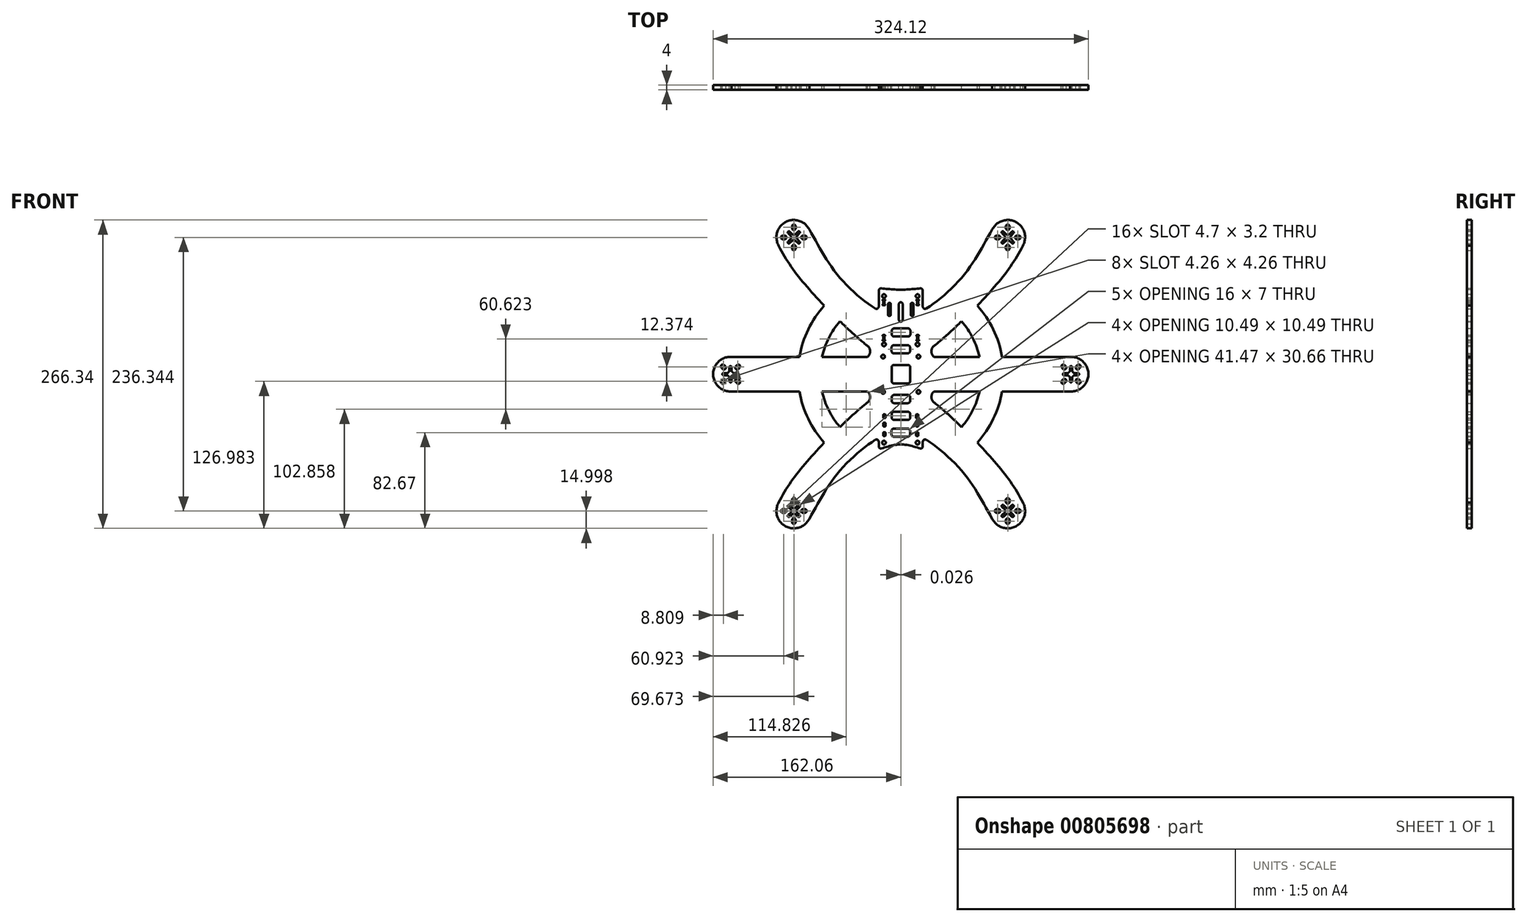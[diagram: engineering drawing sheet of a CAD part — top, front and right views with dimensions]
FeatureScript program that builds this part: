
annotation { "Feature Type Name" : "Feature", "Feature Type Description" : "" }
export const myFeature = defineFeature(function(context is Context, id is Id, definition is map)
    precondition{}
    {
        {
            var Q0;
            Q0=qCreatedBy(makeId("Front.planeOp"),FACE);
            var sketch = newSketch(context, id + "F0", { "sketchPlane" : qUnion([Q0])});
            skLineSegment(sketch, "E0", {"start": v(-266.59, 0) * mm, "end": v(301.68, 0) * mm, "construction": true});
            skCircle(sketch, "E1", {"center": v(-147.06, 0) * mm, "radius": 64.5 * mm, "construction": true});
            skLineSegment(sketch, "E2", {"start": v(0, 169.83) * mm, "end": v(0, -155.18) * mm, "construction": true});
            skCircle(sketch, "E3", {"center": v(-92.39, 118.17) * mm, "radius": 64.5 * mm, "construction": true});
            skCircle(sketch, "E4.MirrorC", {"center": v(-92.39, -118.17) * mm, "radius": 64.5 * mm, "construction": true});
            skCircle(sketch, "E5.MirrorC", {"center": v(92.39, 118.17) * mm, "radius": 64.5 * mm, "construction": true});
            skCircle(sketch, "E6.MirrorC", {"center": v(147.06, 0) * mm, "radius": 64.5 * mm, "construction": true});
            skCircle(sketch, "E7.MirrorC", {"center": v(92.39, -118.17) * mm, "radius": 64.5 * mm, "construction": true});
            skArc(sketch, "E8", {"start": v(-94.8, 118.82) * mm, "mid": v(-94.89, 118.17) * mm, "end": v(-94.8, 117.53) * mm});
            skCircle(sketch, "E9", {"center": v(-92.39, 118.17) * mm, "radius": 15 * mm});
            skArc(sketch, "E10", {"start": v(-148.31, 2.17) * mm, "mid": v(-148.83, 1.77) * mm, "end": v(-149.23, 1.25) * mm});
            skCircle(sketch, "E11", {"center": v(-147.06, 0) * mm, "radius": 15 * mm});
            skCircle(sketch, "E12.MirrorC", {"center": v(-92.39, -118.17) * mm, "radius": 2.5 * mm});
            skCircle(sketch, "E13.MirrorC", {"center": v(-92.39, -118.17) * mm, "radius": 15 * mm});
            skCircle(sketch, "E14.MirrorC", {"center": v(92.39, -118.17) * mm, "radius": 15 * mm});
            skCircle(sketch, "E15.MirrorC", {"center": v(92.39, -118.17) * mm, "radius": 2.5 * mm});
            skCircle(sketch, "E16.MirrorC", {"center": v(147.06, 0) * mm, "radius": 2.5 * mm});
            skCircle(sketch, "E17.MirrorC", {"center": v(147.06, 0) * mm, "radius": 15 * mm});
            skCircle(sketch, "E18.MirrorC", {"center": v(92.39, 118.17) * mm, "radius": 15 * mm});
            skCircle(sketch, "E19.MirrorC", {"center": v(92.39, 118.17) * mm, "radius": 2.5 * mm});
            skLineSegment(sketch, "E20", {"start": v(-92.39, 118.17) * mm, "end": v(92.39, -118.17) * mm, "construction": true});
            skLineSegment(sketch, "E21", {"start": v(92.39, 118.17) * mm, "end": v(-92.39, -118.17) * mm, "construction": true});
            skCircle(sketch, "E22", {"center": v(-15.25, 15.25) * mm, "radius": 1.6 * mm});
            skCircle(sketch, "E23.MirrorC", {"center": v(15.25, 15.25) * mm, "radius": 1.6 * mm});
            skCircle(sketch, "E24.MirrorC", {"center": v(-15.25, -15.25) * mm, "radius": 1.6 * mm});
            skCircle(sketch, "E25.MirrorC", {"center": v(15.25, -15.25) * mm, "radius": 1.6 * mm});
            skLineSegment(sketch, "E26.left", {"start": v(-19.03, 72.1) * mm, "end": v(-19.03, 58.42) * mm});
            skLineSegment(sketch, "E26.right", {"start": v(19.03, 72.1) * mm, "end": v(19.03, 58.42) * mm});
            skPoint(sketch, "E27.orphan", {"position": v(-6.44, 30.02) * mm});
            skLineSegment(sketch, "E28.MirrorCS", {"start": v(-105.57, -111.02) * mm, "end": v(-102.06, -106.7) * mm});
            skLineSegment(sketch, "E29.MirrorCS", {"start": v(-82.26, -129.24) * mm, "end": v(-79, -124.95) * mm});
            skLineSegment(sketch, "E30.MirrorCS", {"start": v(82.26, -129.24) * mm, "end": v(79.02, -124.99) * mm});
            skLineSegment(sketch, "E31.MirrorCS", {"start": v(105.57, -111.02) * mm, "end": v(102.06, -106.7) * mm});
            skPoint(sketch, "E32.orphan", {"position": v(19.03, 13.5) * mm});
            skPoint(sketch, "E33.orphan", {"position": v(19.03, -13.5) * mm});
            skPoint(sketch, "E34.orphan", {"position": v(-19.03, -13.5) * mm});
            skPoint(sketch, "E35.orphan", {"position": v(-19.03, 13.5) * mm});
            skFitSpline(sketch, "E36", {"points": [v(-105.57, 111.02) * mm, v(-74.34, 67.97) * mm, v(-29.36, 24.94) * mm], "startDerivative": vector(48.37, -95.71) * mm, "endDerivative": vector(65.9, -51.43) * mm});
            skFitSpline(sketch, "E37.MirrorCS", {"points": [v(105.57, 111.02) * mm, v(74.34, 67.97) * mm, v(29.36, 24.94) * mm], "startDerivative": vector(-48.37, -95.71) * mm, "endDerivative": vector(-65.9, -51.43) * mm});
            skFitSpline(sketch, "E38.MirrorCS", {"points": [v(-105.57, -111.02) * mm, v(-74.34, -67.97) * mm, v(-29.36, -24.94) * mm], "startDerivative": vector(48.37, 95.71) * mm, "endDerivative": vector(65.9, 51.43) * mm});
            skFitSpline(sketch, "E39.MirrorCS", {"points": [v(105.57, -111.02) * mm, v(74.34, -67.97) * mm, v(29.36, -24.94) * mm], "startDerivative": vector(-48.37, 95.71) * mm, "endDerivative": vector(-65.9, 51.43) * mm});
            skPoint(sketch, "E40.orphan", {"position": v(-27.58, -13.5) * mm});
            skPoint(sketch, "E41.trimOffspring.end.orphan", {"position": v(-27.58, 13.5) * mm});
            skPoint(sketch, "E42.orphan", {"position": v(27.58, -13.5) * mm});
            skPoint(sketch, "E43.trimOffspring.end.orphan", {"position": v(-19.03, -46.2) * mm});
            skPoint(sketch, "E44.orphan", {"position": v(19.03, -46.2) * mm});
            skPoint(sketch, "E45.trimOffspring.end.orphan", {"position": v(19.03, 46.2) * mm});
            skPoint(sketch, "E46.trimOffspring.end.orphan", {"position": v(-19.03, 46.2) * mm});
            skFitSpline(sketch, "E47", {"points": [v(-79.04, 125.02) * mm, v(-55.76, 87.28) * mm, v(-19.03, 54.92) * mm], "startDerivative": vector(44.52, -76.54) * mm, "endDerivative": vector(68.07, -37.92) * mm});
            skFitSpline(sketch, "E48.MirrorCS", {"points": [v(79.04, 125.02) * mm, v(55.76, 87.28) * mm, v(19.03, 54.92) * mm], "startDerivative": vector(-44.52, -76.54) * mm, "endDerivative": vector(-68.07, -37.92) * mm});
            skFitSpline(sketch, "E49.MirrorCS", {"points": [v(-79.04, -125.02) * mm, v(-55.76, -87.28) * mm, v(-19.03, -54.92) * mm], "startDerivative": vector(44.52, 76.54) * mm, "endDerivative": vector(68.07, 37.92) * mm});
            skFitSpline(sketch, "E50.MirrorCS", {"points": [v(79.04, -125.02) * mm, v(55.76, -87.28) * mm, v(19.03, -54.92) * mm], "startDerivative": vector(-44.52, 76.54) * mm, "endDerivative": vector(-68.07, 37.92) * mm});
            skPoint(sketch, "E51.orphan", {"position": v(27.58, 13.5) * mm});
            skLineSegment(sketch, "E52.trimOffspring", {"start": v(-19.03, -58.42) * mm, "end": v(-19.03, -62.32) * mm});
            skLineSegment(sketch, "E53.trimOffspring", {"start": v(19.03, -58.42) * mm, "end": v(19.03, -62.32) * mm});
            skArc(sketch, "E54.filletArc", {"start": v(-19.03, -58.42) * mm, "mid": v(-20.06, -56.67) * mm, "end": v(-22.09, -56.72) * mm});
            skArc(sketch, "E55.filletArc", {"start": v(22.09, -56.72) * mm, "mid": v(20.06, -56.67) * mm, "end": v(19.03, -58.42) * mm});
            skPoint(sketch, "E56.visualSharp", {"position": v(19.03, -64.32) * mm});
            skArc(sketch, "E56.filletArc", {"start": v(17.03, -64.32) * mm, "mid": v(18.44, -63.73) * mm, "end": v(19.03, -62.32) * mm});
            skPoint(sketch, "E57.visualSharp", {"position": v(-19.03, -64.32) * mm});
            skArc(sketch, "E57.filletArc", {"start": v(-19.03, -62.32) * mm, "mid": v(-18.44, -63.73) * mm, "end": v(-17.03, -64.32) * mm});
            skArc(sketch, "E58.filletArc", {"start": v(-22.09, 56.72) * mm, "mid": v(-20.06, 56.67) * mm, "end": v(-19.03, 58.42) * mm});
            skPoint(sketch, "E59.visualSharp", {"position": v(-19.03, 74.1) * mm});
            skArc(sketch, "E59.filletArc", {"start": v(-17.03, 74.1) * mm, "mid": v(-18.44, 73.51) * mm, "end": v(-19.03, 72.1) * mm});
            skPoint(sketch, "E60.visualSharp", {"position": v(19.03, 74.1) * mm});
            skArc(sketch, "E60.filletArc", {"start": v(19.03, 72.1) * mm, "mid": v(18.44, 73.51) * mm, "end": v(17.03, 74.1) * mm});
            skArc(sketch, "E61.filletArc", {"start": v(19.03, 58.42) * mm, "mid": v(20.06, 56.67) * mm, "end": v(22.09, 56.72) * mm});
            skFitSpline(sketch, "E62.trimOffspring", {"points": [v(-105.57, 111.02) * mm, v(-74.34, 67.97) * mm, v(-29.36, 24.94) * mm], "startDerivative": vector(48.37, -95.71) * mm, "endDerivative": vector(65.9, -51.43) * mm});
            skFitSpline(sketch, "E63.trimOffspring", {"points": [v(105.57, 111.02) * mm, v(74.34, 67.97) * mm, v(29.36, 24.94) * mm], "startDerivative": vector(-48.37, -95.71) * mm, "endDerivative": vector(-65.9, -51.43) * mm});
            skFitSpline(sketch, "E64.trimOffspring", {"points": [v(-105.57, -111.02) * mm, v(-74.34, -67.97) * mm, v(-29.36, -24.94) * mm], "startDerivative": vector(48.37, 95.71) * mm, "endDerivative": vector(65.9, 51.43) * mm});
            skFitSpline(sketch, "E65.trimOffspring", {"points": [v(105.57, -111.02) * mm, v(74.34, -67.97) * mm, v(29.36, -24.94) * mm], "startDerivative": vector(-48.37, 95.71) * mm, "endDerivative": vector(-65.9, 51.43) * mm});
            skCircle(sketch, "E66", {"center": v(-14.5, 67.5) * mm, "radius": 1.6 * mm});
            skCircle(sketch, "E67.MirrorC", {"center": v(14.5, 67.5) * mm, "radius": 1.6 * mm});
            skCircle(sketch, "E68", {"center": v(-14.5, 25.75) * mm, "radius": 1.6 * mm});
            skCircle(sketch, "E69.MirrorC", {"center": v(14.5, 25.75) * mm, "radius": 1.6 * mm});
            skCircle(sketch, "E70", {"center": v(-14.5, -59.12) * mm, "radius": 1.6 * mm});
            skCircle(sketch, "E71.MirrorC", {"center": v(14.5, -59.12) * mm, "radius": 1.6 * mm});
            skArc(sketch, "E72", {"start": v(-28.66, 14.98) * mm, "mid": v(-26.5, 20.27) * mm, "end": v(-29.56, 25.1) * mm});
            skArc(sketch, "E73.MirrorCS", {"start": v(28.66, 14.98) * mm, "mid": v(26.5, 20.27) * mm, "end": v(29.56, 25.1) * mm});
            skArc(sketch, "E74.MirrorCS", {"start": v(-28.66, -14.98) * mm, "mid": v(-26.5, -20.27) * mm, "end": v(-29.56, -25.1) * mm});
            skArc(sketch, "E75.MirrorCS", {"start": v(28.66, -14.98) * mm, "mid": v(26.5, -20.27) * mm, "end": v(29.56, -25.1) * mm});
            skLineSegment(sketch, "E76.bottom", {"start": v(-6, -47) * mm, "end": v(6, -47) * mm});
            skLineSegment(sketch, "E76.top", {"start": v(-6, -54) * mm, "end": v(6, -54) * mm});
            skLineSegment(sketch, "E76.left", {"start": v(-8, -49) * mm, "end": v(-8, -52) * mm});
            skLineSegment(sketch, "E76.right", {"start": v(8, -49) * mm, "end": v(8, -52) * mm});
            skLineSegment(sketch, "E77.bottom", {"start": v(-5.85, -32.5) * mm, "end": v(6.15, -32.5) * mm});
            skLineSegment(sketch, "E77.top", {"start": v(-5.85, -39.5) * mm, "end": v(6.15, -39.5) * mm});
            skLineSegment(sketch, "E77.left", {"start": v(-7.85, -34.5) * mm, "end": v(-7.85, -37.5) * mm});
            skLineSegment(sketch, "E77.right", {"start": v(8.15, -34.5) * mm, "end": v(8.15, -37.5) * mm});
            skLineSegment(sketch, "E78.bottom", {"start": v(-5.85, -18) * mm, "end": v(6.15, -18) * mm});
            skLineSegment(sketch, "E78.top", {"start": v(-5.85, -25) * mm, "end": v(6.15, -25) * mm});
            skLineSegment(sketch, "E78.left", {"start": v(-7.85, -20) * mm, "end": v(-7.85, -23) * mm});
            skLineSegment(sketch, "E78.right", {"start": v(8.15, -20) * mm, "end": v(8.15, -23) * mm});
            skLineSegment(sketch, "E79.bottom", {"start": v(-5.97, 25) * mm, "end": v(6.03, 25) * mm});
            skLineSegment(sketch, "E79.top", {"start": v(-5.97, 18) * mm, "end": v(6.03, 18) * mm});
            skLineSegment(sketch, "E79.left", {"start": v(-7.97, 23) * mm, "end": v(-7.97, 20) * mm});
            skLineSegment(sketch, "E79.right", {"start": v(8.03, 23) * mm, "end": v(8.03, 20) * mm});
            skLineSegment(sketch, "E80.bottom", {"start": v(-5.73, 39.5) * mm, "end": v(6.27, 39.5) * mm});
            skLineSegment(sketch, "E80.top", {"start": v(-5.73, 32.5) * mm, "end": v(6.27, 32.5) * mm});
            skLineSegment(sketch, "E80.left", {"start": v(-7.73, 37.5) * mm, "end": v(-7.73, 34.5) * mm});
            skLineSegment(sketch, "E80.right", {"start": v(8.27, 37.5) * mm, "end": v(8.27, 34.5) * mm});
            skLineSegment(sketch, "E81.bottom", {"start": v(-5.85, 8) * mm, "end": v(6.15, 8) * mm});
            skLineSegment(sketch, "E81.top", {"start": v(-5.85, -8) * mm, "end": v(6.15, -8) * mm});
            skLineSegment(sketch, "E81.left", {"start": v(-7.85, 6) * mm, "end": v(-7.85, -6) * mm});
            skLineSegment(sketch, "E81.right", {"start": v(8.15, 6) * mm, "end": v(8.15, -6) * mm});
            skPoint(sketch, "E82.visualSharp", {"position": v(-7.85, 8) * mm});
            skArc(sketch, "E82.filletArc", {"start": v(-5.85, 8) * mm, "mid": v(-7.26, 7.41) * mm, "end": v(-7.85, 6) * mm});
            skPoint(sketch, "E83.visualSharp", {"position": v(8.15, 8) * mm});
            skArc(sketch, "E83.filletArc", {"start": v(8.15, 6) * mm, "mid": v(7.56, 7.41) * mm, "end": v(6.15, 8) * mm});
            skPoint(sketch, "E84.visualSharp", {"position": v(8.15, -8) * mm});
            skArc(sketch, "E84.filletArc", {"start": v(6.15, -8) * mm, "mid": v(7.56, -7.41) * mm, "end": v(8.15, -6) * mm});
            skPoint(sketch, "E85.visualSharp", {"position": v(-7.85, -8) * mm});
            skArc(sketch, "E85.filletArc", {"start": v(-7.85, -6) * mm, "mid": v(-7.26, -7.41) * mm, "end": v(-5.85, -8) * mm});
            skPoint(sketch, "E86.visualSharp", {"position": v(8.15, -18) * mm});
            skArc(sketch, "E86.filletArc", {"start": v(8.15, -20) * mm, "mid": v(7.56, -18.59) * mm, "end": v(6.15, -18) * mm});
            skPoint(sketch, "E87.visualSharp", {"position": v(8.15, -25) * mm});
            skArc(sketch, "E87.filletArc", {"start": v(6.15, -25) * mm, "mid": v(7.56, -24.41) * mm, "end": v(8.15, -23) * mm});
            skPoint(sketch, "E88.visualSharp", {"position": v(-7.85, -25) * mm});
            skArc(sketch, "E88.filletArc", {"start": v(-7.85, -23) * mm, "mid": v(-7.26, -24.41) * mm, "end": v(-5.85, -25) * mm});
            skPoint(sketch, "E89.visualSharp", {"position": v(-7.85, -18) * mm});
            skArc(sketch, "E89.filletArc", {"start": v(-5.85, -18) * mm, "mid": v(-7.26, -18.59) * mm, "end": v(-7.85, -20) * mm});
            skPoint(sketch, "E90.visualSharp", {"position": v(8.15, -32.5) * mm});
            skArc(sketch, "E90.filletArc", {"start": v(8.15, -34.5) * mm, "mid": v(7.56, -33.09) * mm, "end": v(6.15, -32.5) * mm});
            skPoint(sketch, "E91.visualSharp", {"position": v(8.15, -39.5) * mm});
            skArc(sketch, "E91.filletArc", {"start": v(6.15, -39.5) * mm, "mid": v(7.56, -38.91) * mm, "end": v(8.15, -37.5) * mm});
            skPoint(sketch, "E92.visualSharp", {"position": v(-7.85, -39.5) * mm});
            skArc(sketch, "E92.filletArc", {"start": v(-7.85, -37.5) * mm, "mid": v(-7.26, -38.91) * mm, "end": v(-5.85, -39.5) * mm});
            skPoint(sketch, "E93.visualSharp", {"position": v(-7.85, -32.5) * mm});
            skArc(sketch, "E93.filletArc", {"start": v(-5.85, -32.5) * mm, "mid": v(-7.26, -33.09) * mm, "end": v(-7.85, -34.5) * mm});
            skPoint(sketch, "E94.visualSharp", {"position": v(8, -47) * mm});
            skArc(sketch, "E94.filletArc", {"start": v(8, -49) * mm, "mid": v(7.41, -47.59) * mm, "end": v(6, -47) * mm});
            skPoint(sketch, "E95.visualSharp", {"position": v(8, -54) * mm});
            skArc(sketch, "E95.filletArc", {"start": v(6, -54) * mm, "mid": v(7.41, -53.41) * mm, "end": v(8, -52) * mm});
            skPoint(sketch, "E96.visualSharp", {"position": v(-8, -54) * mm});
            skArc(sketch, "E96.filletArc", {"start": v(-8, -52) * mm, "mid": v(-7.41, -53.41) * mm, "end": v(-6, -54) * mm});
            skPoint(sketch, "E97.visualSharp", {"position": v(-8, -47) * mm});
            skArc(sketch, "E97.filletArc", {"start": v(-6, -47) * mm, "mid": v(-7.41, -47.59) * mm, "end": v(-8, -49) * mm});
            skPoint(sketch, "E98.visualSharp", {"position": v(8.03, 18) * mm});
            skArc(sketch, "E98.filletArc", {"start": v(6.03, 18) * mm, "mid": v(7.44, 18.59) * mm, "end": v(8.03, 20) * mm});
            skPoint(sketch, "E99.visualSharp", {"position": v(8.03, 25) * mm});
            skArc(sketch, "E99.filletArc", {"start": v(8.03, 23) * mm, "mid": v(7.44, 24.41) * mm, "end": v(6.03, 25) * mm});
            skPoint(sketch, "E100.visualSharp", {"position": v(-7.97, 25) * mm});
            skArc(sketch, "E100.filletArc", {"start": v(-5.97, 25) * mm, "mid": v(-7.39, 24.41) * mm, "end": v(-7.97, 23) * mm});
            skPoint(sketch, "E101.visualSharp", {"position": v(-7.97, 18) * mm});
            skArc(sketch, "E101.filletArc", {"start": v(-7.97, 20) * mm, "mid": v(-7.39, 18.59) * mm, "end": v(-5.97, 18) * mm});
            skPoint(sketch, "E102.visualSharp", {"position": v(8.27, 39.5) * mm});
            skArc(sketch, "E102.filletArc", {"start": v(8.27, 37.5) * mm, "mid": v(7.69, 38.91) * mm, "end": v(6.27, 39.5) * mm});
            skPoint(sketch, "E103.visualSharp", {"position": v(8.27, 32.5) * mm});
            skArc(sketch, "E103.filletArc", {"start": v(6.27, 32.5) * mm, "mid": v(7.69, 33.09) * mm, "end": v(8.27, 34.5) * mm});
            skPoint(sketch, "E104.visualSharp", {"position": v(-7.73, 32.5) * mm});
            skArc(sketch, "E104.filletArc", {"start": v(-7.73, 34.5) * mm, "mid": v(-7.14, 33.09) * mm, "end": v(-5.73, 32.5) * mm});
            skPoint(sketch, "E105.visualSharp", {"position": v(-7.73, 39.5) * mm});
            skArc(sketch, "E105.filletArc", {"start": v(-5.73, 39.5) * mm, "mid": v(-7.14, 38.91) * mm, "end": v(-7.73, 37.5) * mm});
            skCircle(sketch, "E106", {"center": v(-147.06, 0) * mm, "radius": 8 * mm, "construction": true});
            skCircle(sketch, "E107", {"center": v(-147.06, 0) * mm, "radius": 9.5 * mm, "construction": true});
            skCircle(sketch, "E108", {"center": v(-92.39, 118.17) * mm, "radius": 8 * mm, "construction": true});
            skCircle(sketch, "E109", {"center": v(-92.39, 118.17) * mm, "radius": 9.5 * mm, "construction": true});
            skPoint(sketch, "E110.MirrorCS.start.orphan", {"position": v(-82.26, 129.24) * mm});
            skPoint(sketch, "E111.MirrorCS.start.orphan", {"position": v(82.26, 129.24) * mm});
            skLineSegment(sketch, "E112", {"start": v(-147.82, 14.98) * mm, "end": v(-87.53, 14.98) * mm});
            skLineSegment(sketch, "E113.MirrorCS", {"start": v(-147.82, -14.98) * mm, "end": v(-87.53, -14.98) * mm});
            skLineSegment(sketch, "E114.MirrorCS", {"start": v(147.82, -14.98) * mm, "end": v(87.53, -14.98) * mm});
            skLineSegment(sketch, "E115.MirrorCS", {"start": v(147.82, 14.98) * mm, "end": v(87.53, 14.98) * mm});
            skLineSegment(sketch, "E116", {"start": v(-67.97, 14.98) * mm, "end": v(-28.66, 14.98) * mm});
            skPoint(sketch, "E117.orphan", {"position": v(-32.66, 13.5) * mm});
            skLineSegment(sketch, "E118.MirrorCS", {"start": v(-67.97, -14.98) * mm, "end": v(-28.66, -14.98) * mm});
            skPoint(sketch, "E119.orphan", {"position": v(-32.66, -13.5) * mm});
            skLineSegment(sketch, "E120.MirrorCS", {"start": v(67.97, 14.98) * mm, "end": v(28.66, 14.98) * mm});
            skLineSegment(sketch, "E121.MirrorCS", {"start": v(67.97, -14.98) * mm, "end": v(28.66, -14.98) * mm});
            skPoint(sketch, "E122.orphan", {"position": v(32.66, 13.5) * mm});
            skPoint(sketch, "E123.orphan", {"position": v(32.66, -13.5) * mm});
            skFitSpline(sketch, "E124", {"points": [v(-17.03, 74.1) * mm, v(0, 73.01) * mm, v(17.03, 74.1) * mm], "startDerivative": vector(34.06, -3.26) * mm, "endDerivative": vector(34.06, 3.26) * mm});
            skFitSpline(sketch, "E125", {"points": [v(-17.03, -64.32) * mm, v(0, -60.66) * mm, v(17.03, -64.32) * mm], "startDerivative": vector(34.06, 10.96) * mm, "endDerivative": vector(34.06, -10.96) * mm});
            skArc(sketch, "E126", {"start": v(1.6, 60.5) * mm, "mid": v(0, 62.1) * mm, "end": v(-1.6, 60.5) * mm});
            skArc(sketch, "E127", {"start": v(-1.6, 47) * mm, "mid": v(0, 45.4) * mm, "end": v(1.6, 47) * mm});
            skLineSegment(sketch, "E128", {"start": v(-1.6, 60.5) * mm, "end": v(-1.6, 47) * mm});
            skLineSegment(sketch, "E129.MirrorCS", {"start": v(1.6, 60.5) * mm, "end": v(1.6, 47) * mm});
            skPoint(sketch, "E130.center.orphan", {"position": v(0, 53.75) * mm});
            skLineSegment(sketch, "E131.bottom", {"start": v(-10.32, 61.42) * mm, "end": v(-9.32, 61.42) * mm});
            skLineSegment(sketch, "E131.top", {"start": v(-10.32, 50.42) * mm, "end": v(-9.32, 50.42) * mm});
            skLineSegment(sketch, "E131.left", {"start": v(-10.82, 60.92) * mm, "end": v(-10.82, 50.92) * mm});
            skLineSegment(sketch, "E131.right", {"start": v(-8.82, 60.92) * mm, "end": v(-8.82, 50.92) * mm});
            skPoint(sketch, "E132.visualSharp", {"position": v(-10.82, 61.42) * mm});
            skArc(sketch, "E132.filletArc", {"start": v(-10.32, 61.42) * mm, "mid": v(-10.68, 61.27) * mm, "end": v(-10.82, 60.92) * mm});
            skPoint(sketch, "E133.visualSharp", {"position": v(-8.82, 61.42) * mm});
            skArc(sketch, "E133.filletArc", {"start": v(-8.82, 60.92) * mm, "mid": v(-8.97, 61.27) * mm, "end": v(-9.32, 61.42) * mm});
            skPoint(sketch, "E134.visualSharp", {"position": v(-8.82, 50.42) * mm});
            skArc(sketch, "E134.filletArc", {"start": v(-9.32, 50.42) * mm, "mid": v(-8.97, 50.56) * mm, "end": v(-8.82, 50.92) * mm});
            skPoint(sketch, "E135.visualSharp", {"position": v(-10.82, 50.42) * mm});
            skArc(sketch, "E135.filletArc", {"start": v(-10.82, 50.92) * mm, "mid": v(-10.68, 50.56) * mm, "end": v(-10.32, 50.42) * mm});
            skArc(sketch, "E136.MirrorCS", {"start": v(8.82, 60.92) * mm, "mid": v(8.97, 61.27) * mm, "end": v(9.32, 61.42) * mm});
            skLineSegment(sketch, "E137.MirrorCS", {"start": v(10.32, 50.42) * mm, "end": v(9.32, 50.42) * mm});
            skLineSegment(sketch, "E138.MirrorCS", {"start": v(10.32, 61.42) * mm, "end": v(9.32, 61.42) * mm});
            skArc(sketch, "E139.MirrorCS", {"start": v(10.32, 61.42) * mm, "mid": v(10.68, 61.27) * mm, "end": v(10.82, 60.92) * mm});
            skArc(sketch, "E140.MirrorCS", {"start": v(9.32, 50.42) * mm, "mid": v(8.97, 50.56) * mm, "end": v(8.82, 50.92) * mm});
            skArc(sketch, "E141.MirrorCS", {"start": v(10.82, 50.92) * mm, "mid": v(10.68, 50.56) * mm, "end": v(10.32, 50.42) * mm});
            skLineSegment(sketch, "E142.MirrorCS", {"start": v(8.82, 60.92) * mm, "end": v(8.82, 50.92) * mm});
            skPoint(sketch, "E143.MirrorP", {"position": v(10.82, 61.42) * mm});
            skLineSegment(sketch, "E144.MirrorCS", {"start": v(10.82, 60.92) * mm, "end": v(10.82, 50.92) * mm});
            skPoint(sketch, "E145.MirrorP", {"position": v(8.82, 61.42) * mm});
            skPoint(sketch, "E146.MirrorP", {"position": v(10.82, 50.42) * mm});
            skPoint(sketch, "E147.MirrorP", {"position": v(8.82, 50.42) * mm});
            skCircle(sketch, "E148.MirrorC", {"center": v(92.39, 118.17) * mm, "radius": 9.5 * mm, "construction": true});
            skCircle(sketch, "E149.MirrorC", {"center": v(92.39, 118.17) * mm, "radius": 8 * mm, "construction": true});
            skCircle(sketch, "E150.MirrorC", {"center": v(-92.39, -118.17) * mm, "radius": 9.5 * mm, "construction": true});
            skCircle(sketch, "E151.MirrorC", {"center": v(-92.39, -118.17) * mm, "radius": 8 * mm, "construction": true});
            skCircle(sketch, "E152.MirrorC", {"center": v(92.39, -118.17) * mm, "radius": 9.5 * mm, "construction": true});
            skCircle(sketch, "E153.MirrorC", {"center": v(92.39, -118.17) * mm, "radius": 8 * mm, "construction": true});
            skCircle(sketch, "E154.MirrorC", {"center": v(147.06, 0) * mm, "radius": 9.5 * mm, "construction": true});
            skCircle(sketch, "E155.MirrorC", {"center": v(147.06, 0) * mm, "radius": 8 * mm, "construction": true});
            skPoint(sketch, "E156.orphan", {"position": v(-85.2, 14.98) * mm});
            skPoint(sketch, "E157.orphan", {"position": v(-85.2, -14.98) * mm});
            skPoint(sketch, "E158.orphan", {"position": v(85.2, -14.98) * mm});
            skArc(sketch, "E159", {"start": v(-67.97, -14.98) * mm, "mid": v(-62.18, -31.28) * mm, "end": v(-52.55, -45.64) * mm});
            skArc(sketch, "E160", {"start": v(-87.53, -14.98) * mm, "mid": v(-79.96, -38.63) * mm, "end": v(-66.14, -59.26) * mm});
            skPoint(sketch, "E161.orphan", {"position": v(-55.52, 48.54) * mm});
            skLineSegment(sketch, "E162.trimOffspring", {"start": v(-85.2, 14.98) * mm, "end": v(-84.33, 14.98) * mm});
            skLineSegment(sketch, "E163.trimOffspring", {"start": v(-85.2, -14.98) * mm, "end": v(-84.33, -14.98) * mm});
            skArc(sketch, "E164.trimOffspring", {"start": v(-52.55, 45.64) * mm, "mid": v(-62.18, 31.28) * mm, "end": v(-67.97, 14.98) * mm});
            skArc(sketch, "E165.trimOffspring", {"start": v(-66.14, 59.26) * mm, "mid": v(-79.96, 38.63) * mm, "end": v(-87.53, 14.98) * mm});
            skPoint(sketch, "E166.orphan", {"position": v(55.52, 48.54) * mm});
            skArc(sketch, "E167.trimOffspring", {"start": v(67.97, 14.98) * mm, "mid": v(62.18, 31.28) * mm, "end": v(52.55, 45.64) * mm});
            skArc(sketch, "E168.trimOffspring", {"start": v(87.53, 14.98) * mm, "mid": v(79.96, 38.63) * mm, "end": v(66.14, 59.26) * mm});
            skLineSegment(sketch, "E169.trimOffspring", {"start": v(85.2, 14.98) * mm, "end": v(84.33, 14.98) * mm});
            skLineSegment(sketch, "E170.trimOffspring", {"start": v(85.2, -14.98) * mm, "end": v(84.33, -14.98) * mm});
            skPoint(sketch, "E171.orphan", {"position": v(55.52, -48.54) * mm});
            skArc(sketch, "E172.trimOffspring", {"start": v(52.55, -45.64) * mm, "mid": v(62.18, -31.28) * mm, "end": v(67.97, -14.98) * mm});
            skArc(sketch, "E173.trimOffspring", {"start": v(66.14, -59.26) * mm, "mid": v(79.96, -38.63) * mm, "end": v(87.53, -14.98) * mm});
            skLineSegment(sketch, "E174", {"start": v(-147.06, 18.16) * mm, "end": v(-147.06, -18.32) * mm, "construction": true});
            skLineSegment(sketch, "E175", {"start": v(-163.44, 0) * mm, "end": v(-130.7, 0) * mm, "construction": true});
            skLineSegment(sketch, "E176", {"start": v(-162.22, -15.16) * mm, "end": v(-131.9, 15.16) * mm, "construction": true});
            skLineSegment(sketch, "E177.MirrorCS", {"start": v(-131.9, -15.16) * mm, "end": v(-162.22, 15.16) * mm, "construction": true});
            skArc(sketch, "E178", {"start": v(-146.06, 6) * mm, "mid": v(-147.06, 7) * mm, "end": v(-148.06, 6) * mm});
            skLineSegment(sketch, "E179", {"start": v(-148.06, 6) * mm, "end": v(-148.06, 2.6) * mm});
            skLineSegment(sketch, "E180.MirrorCS", {"start": v(-146.06, 6) * mm, "end": v(-146.06, 2.6) * mm});
            skLineSegment(sketch, "E181.MirrorCS", {"start": v(-148.06, -6) * mm, "end": v(-148.06, -2.6) * mm});
            skLineSegment(sketch, "E182.MirrorCS", {"start": v(-146.06, -6) * mm, "end": v(-146.06, -2.6) * mm});
            skArc(sketch, "E183.MirrorCS", {"start": v(-146.06, -6) * mm, "mid": v(-147.06, -7) * mm, "end": v(-148.06, -6) * mm});
            skArc(sketch, "E184", {"start": v(-141.06, -1) * mm, "mid": v(-140.06, 0) * mm, "end": v(-141.06, 1) * mm});
            skLineSegment(sketch, "E185", {"start": v(-141.06, 1) * mm, "end": v(-144.47, 1) * mm});
            skLineSegment(sketch, "E186.MirrorCS", {"start": v(-141.06, -1) * mm, "end": v(-144.77, -1) * mm});
            skLineSegment(sketch, "E187.MirrorCS", {"start": v(-141.06, -1) * mm, "end": v(-144.47, -1) * mm});
            skArc(sketch, "E188.trimOffspring", {"start": v(-144.9, 1.25) * mm, "mid": v(-145.3, 1.77) * mm, "end": v(-145.81, 2.17) * mm});
            skLineSegment(sketch, "E189.MirrorCS", {"start": v(-153.06, 1) * mm, "end": v(-149.66, 1) * mm});
            skArc(sketch, "E190.MirrorCS", {"start": v(-153.06, -1) * mm, "mid": v(-154.06, 0) * mm, "end": v(-153.06, 1) * mm});
            skLineSegment(sketch, "E191.MirrorCS", {"start": v(-153.06, -1) * mm, "end": v(-149.66, -1) * mm});
            skArc(sketch, "E192.trimOffspring", {"start": v(-149.23, -1.25) * mm, "mid": v(-148.83, -1.77) * mm, "end": v(-148.31, -2.17) * mm});
            skArc(sketch, "E193.trimOffspring", {"start": v(-145.81, -2.17) * mm, "mid": v(-145.3, -1.77) * mm, "end": v(-144.9, -1.25) * mm});
            skPoint(sketch, "E194.visualSharp", {"position": v(-148.06, 2.3) * mm});
            skArc(sketch, "E194.filletArc", {"start": v(-148.31, 2.17) * mm, "mid": v(-148.13, 2.35) * mm, "end": v(-148.06, 2.6) * mm});
            skPoint(sketch, "E195.visualSharp", {"position": v(-149.36, 1) * mm});
            skArc(sketch, "E195.filletArc", {"start": v(-149.66, 1) * mm, "mid": v(-149.41, 1.07) * mm, "end": v(-149.23, 1.25) * mm});
            skPoint(sketch, "E196.visualSharp", {"position": v(-149.36, -1) * mm});
            skArc(sketch, "E196.filletArc", {"start": v(-149.23, -1.25) * mm, "mid": v(-149.41, -1.07) * mm, "end": v(-149.66, -1) * mm});
            skPoint(sketch, "E197.visualSharp", {"position": v(-148.06, -2.3) * mm});
            skArc(sketch, "E197.filletArc", {"start": v(-148.06, -2.6) * mm, "mid": v(-148.13, -2.35) * mm, "end": v(-148.31, -2.17) * mm});
            skPoint(sketch, "E198.visualSharp", {"position": v(-146.06, -2.3) * mm});
            skArc(sketch, "E198.filletArc", {"start": v(-145.81, -2.17) * mm, "mid": v(-146, -2.35) * mm, "end": v(-146.06, -2.6) * mm});
            skPoint(sketch, "E199.visualSharp", {"position": v(-144.77, -1) * mm});
            skArc(sketch, "E199.filletArc", {"start": v(-144.47, -1) * mm, "mid": v(-144.72, -1.07) * mm, "end": v(-144.9, -1.25) * mm});
            skPoint(sketch, "E200.visualSharp", {"position": v(-144.77, 1) * mm});
            skArc(sketch, "E200.filletArc", {"start": v(-144.9, 1.25) * mm, "mid": v(-144.72, 1.07) * mm, "end": v(-144.47, 1) * mm});
            skPoint(sketch, "E201.visualSharp", {"position": v(-146.06, 2.3) * mm});
            skArc(sketch, "E201.filletArc", {"start": v(-146.06, 2.6) * mm, "mid": v(-146, 2.35) * mm, "end": v(-145.81, 2.17) * mm});
            skArc(sketch, "E202", {"start": v(-152.65, 7.85) * mm, "mid": v(-154.91, 7.85) * mm, "end": v(-154.91, 5.59) * mm});
            skLineSegment(sketch, "E203", {"start": v(-152.65, 7.85) * mm, "end": v(-151.59, 6.79) * mm});
            skLineSegment(sketch, "E204.MirrorCS", {"start": v(-154.91, 5.59) * mm, "end": v(-153.85, 4.53) * mm});
            skArc(sketch, "E205.trimOffspring", {"start": v(-153.85, 4.53) * mm, "mid": v(-151.59, 4.53) * mm, "end": v(-151.59, 6.79) * mm});
            skArc(sketch, "E206.MirrorCS", {"start": v(-141.48, 7.85) * mm, "mid": v(-139.22, 7.85) * mm, "end": v(-139.22, 5.59) * mm});
            skLineSegment(sketch, "E207.MirrorCS", {"start": v(-141.48, 7.85) * mm, "end": v(-142.54, 6.79) * mm});
            skLineSegment(sketch, "E208.MirrorCS", {"start": v(-139.22, 5.59) * mm, "end": v(-140.28, 4.53) * mm});
            skArc(sketch, "E209.MirrorCS", {"start": v(-140.28, 4.53) * mm, "mid": v(-142.54, 4.53) * mm, "end": v(-142.54, 6.79) * mm});
            skArc(sketch, "E210.MirrorCS", {"start": v(-152.65, -7.85) * mm, "mid": v(-154.91, -7.85) * mm, "end": v(-154.91, -5.59) * mm});
            skLineSegment(sketch, "E211.MirrorCS", {"start": v(-154.91, -5.59) * mm, "end": v(-153.85, -4.53) * mm});
            skArc(sketch, "E212.MirrorCS", {"start": v(-153.85, -4.53) * mm, "mid": v(-151.59, -4.53) * mm, "end": v(-151.59, -6.79) * mm});
            skLineSegment(sketch, "E213.MirrorCS", {"start": v(-152.65, -7.85) * mm, "end": v(-151.59, -6.79) * mm});
            skLineSegment(sketch, "E214.MirrorCS", {"start": v(-141.48, -7.85) * mm, "end": v(-142.54, -6.79) * mm});
            skArc(sketch, "E215.MirrorCS", {"start": v(-140.28, -4.53) * mm, "mid": v(-142.54, -4.53) * mm, "end": v(-142.54, -6.79) * mm});
            skLineSegment(sketch, "E216.MirrorCS", {"start": v(-139.22, -5.59) * mm, "end": v(-140.28, -4.53) * mm});
            skArc(sketch, "E217.MirrorCS", {"start": v(-141.48, -7.85) * mm, "mid": v(-139.22, -7.85) * mm, "end": v(-139.22, -5.59) * mm});
            skArc(sketch, "E218.MirrorCS", {"start": v(145.81, -2.17) * mm, "mid": v(146, -2.35) * mm, "end": v(146.06, -2.6) * mm});
            skArc(sketch, "E219.MirrorCS", {"start": v(144.47, -1) * mm, "mid": v(144.72, -1.07) * mm, "end": v(144.9, -1.25) * mm});
            skArc(sketch, "E220.MirrorCS", {"start": v(144.9, 1.25) * mm, "mid": v(144.72, 1.07) * mm, "end": v(144.47, 1) * mm});
            skArc(sketch, "E221.MirrorCS", {"start": v(148.31, 2.17) * mm, "mid": v(148.83, 1.77) * mm, "end": v(149.23, 1.25) * mm});
            skArc(sketch, "E222.MirrorCS", {"start": v(148.06, -2.6) * mm, "mid": v(148.13, -2.35) * mm, "end": v(148.31, -2.17) * mm});
            skArc(sketch, "E223.MirrorCS", {"start": v(145.81, -2.17) * mm, "mid": v(145.3, -1.77) * mm, "end": v(144.9, -1.25) * mm});
            skArc(sketch, "E224.MirrorCS", {"start": v(144.9, 1.25) * mm, "mid": v(145.3, 1.77) * mm, "end": v(145.81, 2.17) * mm});
            skArc(sketch, "E225.MirrorCS", {"start": v(149.23, -1.25) * mm, "mid": v(149.41, -1.07) * mm, "end": v(149.66, -1) * mm});
            skArc(sketch, "E226.MirrorCS", {"start": v(146.06, 2.6) * mm, "mid": v(146, 2.35) * mm, "end": v(145.81, 2.17) * mm});
            skArc(sketch, "E227.MirrorCS", {"start": v(149.23, -1.25) * mm, "mid": v(148.83, -1.77) * mm, "end": v(148.31, -2.17) * mm});
            skArc(sketch, "E228.MirrorCS", {"start": v(149.66, 1) * mm, "mid": v(149.41, 1.07) * mm, "end": v(149.23, 1.25) * mm});
            skArc(sketch, "E229.MirrorCS", {"start": v(148.31, 2.17) * mm, "mid": v(148.13, 2.35) * mm, "end": v(148.06, 2.6) * mm});
            skLineSegment(sketch, "E230.MirrorCS", {"start": v(152.65, 7.85) * mm, "end": v(151.59, 6.79) * mm});
            skLineSegment(sketch, "E231.MirrorCS", {"start": v(139.22, 5.59) * mm, "end": v(140.28, 4.53) * mm});
            skLineSegment(sketch, "E232.MirrorCS", {"start": v(154.91, 5.59) * mm, "end": v(153.85, 4.53) * mm});
            skLineSegment(sketch, "E233.MirrorCS", {"start": v(141.06, -1) * mm, "end": v(144.77, -1) * mm});
            skLineSegment(sketch, "E234.MirrorCS", {"start": v(153.06, -1) * mm, "end": v(149.66, -1) * mm});
            skLineSegment(sketch, "E235.MirrorCS", {"start": v(148.06, -6) * mm, "end": v(148.06, -2.6) * mm});
            skLineSegment(sketch, "E236.MirrorCS", {"start": v(148.06, 6) * mm, "end": v(148.06, 2.6) * mm});
            skLineSegment(sketch, "E237.MirrorCS", {"start": v(141.48, -7.85) * mm, "end": v(142.54, -6.79) * mm});
            skLineSegment(sketch, "E238.MirrorCS", {"start": v(146.06, -6) * mm, "end": v(146.06, -2.6) * mm});
            skArc(sketch, "E239.MirrorCS", {"start": v(140.28, -4.53) * mm, "mid": v(142.54, -4.53) * mm, "end": v(142.54, -6.79) * mm});
            skLineSegment(sketch, "E240.MirrorCS", {"start": v(153.06, 1) * mm, "end": v(149.66, 1) * mm});
            skPoint(sketch, "E241.MirrorP", {"position": v(149.36, -1) * mm});
            skPoint(sketch, "E242.MirrorP", {"position": v(148.06, 2.3) * mm});
            skArc(sketch, "E243.MirrorCS", {"start": v(152.65, 7.85) * mm, "mid": v(154.91, 7.85) * mm, "end": v(154.91, 5.59) * mm});
            skPoint(sketch, "E244.MirrorP", {"position": v(148.06, -2.3) * mm});
            skArc(sketch, "E245.MirrorCS", {"start": v(153.06, -1) * mm, "mid": v(154.06, 0) * mm, "end": v(153.06, 1) * mm});
            skLineSegment(sketch, "E246.MirrorCS", {"start": v(141.06, -1) * mm, "end": v(144.47, -1) * mm});
            skPoint(sketch, "E247.MirrorP", {"position": v(146.06, -2.3) * mm});
            skPoint(sketch, "E248.MirrorP", {"position": v(146.06, 2.3) * mm});
            skLineSegment(sketch, "E249.MirrorCS", {"start": v(152.65, -7.85) * mm, "end": v(151.59, -6.79) * mm});
            skArc(sketch, "E250.MirrorCS", {"start": v(146.06, -6) * mm, "mid": v(147.06, -7) * mm, "end": v(148.06, -6) * mm});
            skLineSegment(sketch, "E251.MirrorCS", {"start": v(141.48, 7.85) * mm, "end": v(142.54, 6.79) * mm});
            skArc(sketch, "E252.MirrorCS", {"start": v(153.85, 4.53) * mm, "mid": v(151.59, 4.53) * mm, "end": v(151.59, 6.79) * mm});
            skArc(sketch, "E253.MirrorCS", {"start": v(140.28, 4.53) * mm, "mid": v(142.54, 4.53) * mm, "end": v(142.54, 6.79) * mm});
            skLineSegment(sketch, "E254.MirrorCS", {"start": v(146.06, 6) * mm, "end": v(146.06, 2.6) * mm});
            skArc(sketch, "E255.MirrorCS", {"start": v(153.85, -4.53) * mm, "mid": v(151.59, -4.53) * mm, "end": v(151.59, -6.79) * mm});
            skArc(sketch, "E256.MirrorCS", {"start": v(141.48, -7.85) * mm, "mid": v(139.22, -7.85) * mm, "end": v(139.22, -5.59) * mm});
            skLineSegment(sketch, "E257.MirrorCS", {"start": v(141.06, 1) * mm, "end": v(144.47, 1) * mm});
            skArc(sketch, "E258.MirrorCS", {"start": v(141.06, -1) * mm, "mid": v(140.06, 0) * mm, "end": v(141.06, 1) * mm});
            skLineSegment(sketch, "E259.MirrorCS", {"start": v(154.91, -5.59) * mm, "end": v(153.85, -4.53) * mm});
            skLineSegment(sketch, "E260.MirrorCS", {"start": v(139.22, -5.59) * mm, "end": v(140.28, -4.53) * mm});
            skPoint(sketch, "E261.MirrorP", {"position": v(144.77, -1) * mm});
            skPoint(sketch, "E262.MirrorP", {"position": v(149.36, 1) * mm});
            skPoint(sketch, "E263.MirrorP", {"position": v(144.77, 1) * mm});
            skArc(sketch, "E264.MirrorCS", {"start": v(152.65, -7.85) * mm, "mid": v(154.91, -7.85) * mm, "end": v(154.91, -5.59) * mm});
            skArc(sketch, "E265.MirrorCS", {"start": v(141.48, 7.85) * mm, "mid": v(139.22, 7.85) * mm, "end": v(139.22, 5.59) * mm});
            skArc(sketch, "E266.MirrorCS", {"start": v(146.06, 6) * mm, "mid": v(147.06, 7) * mm, "end": v(148.06, 6) * mm});
            skLineSegment(sketch, "E267", {"start": v(-15.21, 33.8) * mm, "end": v(-14.1, 33.8) * mm});
            skLineSegment(sketch, "E268", {"start": v(-13.6, 33.3) * mm, "end": v(-13.6, 33.3) * mm});
            skLineSegment(sketch, "E269", {"start": v(-14.1, 32.8) * mm, "end": v(-14.15, 32.8) * mm});
            skLineSegment(sketch, "E270", {"start": v(-14.15, 32.8) * mm, "end": v(-14.15, 29.76) * mm});
            skLineSegment(sketch, "E271", {"start": v(-14.15, 29.76) * mm, "end": v(-14.1, 29.76) * mm});
            skLineSegment(sketch, "E272", {"start": v(-13.6, 29.26) * mm, "end": v(-13.6, 29.26) * mm});
            skLineSegment(sketch, "E273", {"start": v(-14.1, 28.76) * mm, "end": v(-15.21, 28.76) * mm});
            skLineSegment(sketch, "E274", {"start": v(-15.71, 29.26) * mm, "end": v(-15.71, 29.26) * mm});
            skLineSegment(sketch, "E275", {"start": v(-15.21, 29.76) * mm, "end": v(-15.15, 29.76) * mm});
            skLineSegment(sketch, "E276", {"start": v(-15.15, 29.76) * mm, "end": v(-15.15, 32.8) * mm});
            skLineSegment(sketch, "E277", {"start": v(-15.15, 32.8) * mm, "end": v(-15.21, 32.8) * mm});
            skLineSegment(sketch, "E278", {"start": v(-15.71, 33.3) * mm, "end": v(-15.71, 33.3) * mm});
            skPoint(sketch, "E279.visualSharp", {"position": v(-15.71, 33.8) * mm});
            skArc(sketch, "E279.filletArc", {"start": v(-15.21, 33.8) * mm, "mid": v(-15.56, 33.65) * mm, "end": v(-15.71, 33.3) * mm});
            skPoint(sketch, "E280.visualSharp", {"position": v(-15.71, 32.8) * mm});
            skArc(sketch, "E280.filletArc", {"start": v(-15.71, 33.3) * mm, "mid": v(-15.56, 32.94) * mm, "end": v(-15.21, 32.8) * mm});
            skPoint(sketch, "E281.visualSharp", {"position": v(-13.6, 33.8) * mm});
            skArc(sketch, "E281.filletArc", {"start": v(-13.6, 33.3) * mm, "mid": v(-13.74, 33.65) * mm, "end": v(-14.1, 33.8) * mm});
            skPoint(sketch, "E282.visualSharp", {"position": v(-13.6, 32.8) * mm});
            skArc(sketch, "E282.filletArc", {"start": v(-14.1, 32.8) * mm, "mid": v(-13.74, 32.94) * mm, "end": v(-13.6, 33.3) * mm});
            skPoint(sketch, "E283.visualSharp", {"position": v(-13.6, 29.76) * mm});
            skArc(sketch, "E283.filletArc", {"start": v(-13.6, 29.26) * mm, "mid": v(-13.74, 29.62) * mm, "end": v(-14.1, 29.76) * mm});
            skPoint(sketch, "E284.visualSharp", {"position": v(-13.6, 28.76) * mm});
            skArc(sketch, "E284.filletArc", {"start": v(-14.1, 28.76) * mm, "mid": v(-13.74, 28.9) * mm, "end": v(-13.6, 29.26) * mm});
            skPoint(sketch, "E285.visualSharp", {"position": v(-15.71, 29.76) * mm});
            skArc(sketch, "E285.filletArc", {"start": v(-15.21, 29.76) * mm, "mid": v(-15.56, 29.62) * mm, "end": v(-15.71, 29.26) * mm});
            skPoint(sketch, "E286.visualSharp", {"position": v(-15.71, 28.76) * mm});
            skArc(sketch, "E286.filletArc", {"start": v(-15.71, 29.26) * mm, "mid": v(-15.56, 28.9) * mm, "end": v(-15.21, 28.76) * mm});
            skLineSegment(sketch, "E287", {"start": v(-29.23, 46.63) * mm, "end": v(29.48, 46.63) * mm, "construction": true});
            skLineSegment(sketch, "E288.MirrorCS", {"start": v(-14.15, 63.5) * mm, "end": v(-14.1, 63.5) * mm});
            skArc(sketch, "E289.MirrorCS", {"start": v(-14.1, 60.47) * mm, "mid": v(-13.74, 60.32) * mm, "end": v(-13.6, 59.97) * mm});
            skArc(sketch, "E290.MirrorCS", {"start": v(-13.6, 59.97) * mm, "mid": v(-13.74, 59.62) * mm, "end": v(-14.1, 59.47) * mm});
            skArc(sketch, "E291.MirrorCS", {"start": v(-15.71, 59.97) * mm, "mid": v(-15.56, 60.32) * mm, "end": v(-15.21, 60.47) * mm});
            skArc(sketch, "E292.MirrorCS", {"start": v(-15.21, 59.47) * mm, "mid": v(-15.56, 59.62) * mm, "end": v(-15.71, 59.97) * mm});
            skLineSegment(sketch, "E293.MirrorCS", {"start": v(-15.15, 60.47) * mm, "end": v(-15.21, 60.47) * mm});
            skLineSegment(sketch, "E294.MirrorCS", {"start": v(-15.21, 63.5) * mm, "end": v(-15.15, 63.5) * mm});
            skLineSegment(sketch, "E295.MirrorCS", {"start": v(-14.1, 60.47) * mm, "end": v(-14.15, 60.47) * mm});
            skLineSegment(sketch, "E296.MirrorCS", {"start": v(-15.21, 59.47) * mm, "end": v(-14.1, 59.47) * mm});
            skArc(sketch, "E297.MirrorCS", {"start": v(-15.21, 63.5) * mm, "mid": v(-15.56, 63.65) * mm, "end": v(-15.71, 64) * mm});
            skArc(sketch, "E298.MirrorCS", {"start": v(-13.6, 64) * mm, "mid": v(-13.74, 63.65) * mm, "end": v(-14.1, 63.5) * mm});
            skLineSegment(sketch, "E299.MirrorCS", {"start": v(-14.1, 64.5) * mm, "end": v(-15.21, 64.5) * mm});
            skArc(sketch, "E300.MirrorCS", {"start": v(-15.71, 64) * mm, "mid": v(-15.56, 64.35) * mm, "end": v(-15.21, 64.5) * mm});
            skArc(sketch, "E301.MirrorCS", {"start": v(-14.1, 64.5) * mm, "mid": v(-13.74, 64.35) * mm, "end": v(-13.6, 64) * mm});
            skLineSegment(sketch, "E302.MirrorCS", {"start": v(-15.71, 59.97) * mm, "end": v(-15.71, 59.97) * mm});
            skLineSegment(sketch, "E303.MirrorCS", {"start": v(-15.71, 64) * mm, "end": v(-15.71, 64) * mm});
            skLineSegment(sketch, "E304.MirrorCS", {"start": v(-13.6, 64) * mm, "end": v(-13.6, 64) * mm});
            skLineSegment(sketch, "E305.MirrorCS", {"start": v(-13.6, 59.97) * mm, "end": v(-13.6, 59.97) * mm});
            skPoint(sketch, "E306.MirrorP", {"position": v(-15.71, 64.5) * mm});
            skPoint(sketch, "E307.MirrorP", {"position": v(-15.71, 63.5) * mm});
            skPoint(sketch, "E308.MirrorP", {"position": v(-13.6, 64.5) * mm});
            skLineSegment(sketch, "E309.MirrorCS", {"start": v(-15.15, 63.5) * mm, "end": v(-15.15, 60.47) * mm});
            skPoint(sketch, "E310.MirrorP", {"position": v(-13.6, 63.5) * mm});
            skPoint(sketch, "E311.MirrorP", {"position": v(-13.6, 60.47) * mm});
            skLineSegment(sketch, "E312.MirrorCS", {"start": v(-14.15, 60.47) * mm, "end": v(-14.15, 63.5) * mm});
            skPoint(sketch, "E313.MirrorP", {"position": v(-13.6, 59.47) * mm});
            skPoint(sketch, "E314.MirrorP", {"position": v(-15.71, 60.47) * mm});
            skPoint(sketch, "E315.MirrorP", {"position": v(-15.71, 59.47) * mm});
            skArc(sketch, "E316.MirrorCS", {"start": v(14.1, 60.47) * mm, "mid": v(13.74, 60.32) * mm, "end": v(13.6, 59.97) * mm});
            skArc(sketch, "E317.MirrorCS", {"start": v(13.6, 64) * mm, "mid": v(13.74, 63.65) * mm, "end": v(14.1, 63.5) * mm});
            skLineSegment(sketch, "E318.MirrorCS", {"start": v(14.15, 63.5) * mm, "end": v(14.1, 63.5) * mm});
            skArc(sketch, "E319.MirrorCS", {"start": v(15.71, 59.97) * mm, "mid": v(15.56, 60.32) * mm, "end": v(15.21, 60.47) * mm});
            skLineSegment(sketch, "E320.MirrorCS", {"start": v(15.15, 60.47) * mm, "end": v(15.21, 60.47) * mm});
            skLineSegment(sketch, "E321.MirrorCS", {"start": v(15.21, 63.5) * mm, "end": v(15.15, 63.5) * mm});
            skLineSegment(sketch, "E322.MirrorCS", {"start": v(14.1, 60.47) * mm, "end": v(14.15, 60.47) * mm});
            skArc(sketch, "E323.MirrorCS", {"start": v(15.21, 63.5) * mm, "mid": v(15.56, 63.65) * mm, "end": v(15.71, 64) * mm});
            skArc(sketch, "E324.MirrorCS", {"start": v(15.71, 64) * mm, "mid": v(15.56, 64.35) * mm, "end": v(15.21, 64.5) * mm});
            skArc(sketch, "E325.MirrorCS", {"start": v(14.1, 64.5) * mm, "mid": v(13.74, 64.35) * mm, "end": v(13.6, 64) * mm});
            skArc(sketch, "E326.MirrorCS", {"start": v(13.6, 59.97) * mm, "mid": v(13.74, 59.62) * mm, "end": v(14.1, 59.47) * mm});
            skArc(sketch, "E327.MirrorCS", {"start": v(15.21, 59.47) * mm, "mid": v(15.56, 59.62) * mm, "end": v(15.71, 59.97) * mm});
            skLineSegment(sketch, "E328.MirrorCS", {"start": v(15.71, 59.97) * mm, "end": v(15.71, 59.97) * mm});
            skLineSegment(sketch, "E329.MirrorCS", {"start": v(15.71, 64) * mm, "end": v(15.71, 64) * mm});
            skLineSegment(sketch, "E330.MirrorCS", {"start": v(13.6, 64) * mm, "end": v(13.6, 64) * mm});
            skLineSegment(sketch, "E331.MirrorCS", {"start": v(13.6, 59.97) * mm, "end": v(13.6, 59.97) * mm});
            skPoint(sketch, "E332.MirrorP", {"position": v(15.71, 59.47) * mm});
            skLineSegment(sketch, "E333.MirrorCS", {"start": v(14.1, 64.5) * mm, "end": v(15.21, 64.5) * mm});
            skLineSegment(sketch, "E334.MirrorCS", {"start": v(15.15, 63.5) * mm, "end": v(15.15, 60.47) * mm});
            skLineSegment(sketch, "E335.MirrorCS", {"start": v(14.15, 60.47) * mm, "end": v(14.15, 63.5) * mm});
            skPoint(sketch, "E336.MirrorP", {"position": v(15.71, 64.5) * mm});
            skPoint(sketch, "E337.MirrorP", {"position": v(15.71, 63.5) * mm});
            skPoint(sketch, "E338.MirrorP", {"position": v(13.6, 64.5) * mm});
            skPoint(sketch, "E339.MirrorP", {"position": v(13.6, 63.5) * mm});
            skPoint(sketch, "E340.MirrorP", {"position": v(13.6, 60.47) * mm});
            skLineSegment(sketch, "E341.MirrorCS", {"start": v(15.21, 59.47) * mm, "end": v(14.1, 59.47) * mm});
            skPoint(sketch, "E342.MirrorP", {"position": v(13.6, 59.47) * mm});
            skPoint(sketch, "E343.MirrorP", {"position": v(15.71, 60.47) * mm});
            skArc(sketch, "E344.MirrorCS", {"start": v(13.6, 29.26) * mm, "mid": v(13.74, 29.62) * mm, "end": v(14.1, 29.76) * mm});
            skArc(sketch, "E345.MirrorCS", {"start": v(14.1, 32.8) * mm, "mid": v(13.74, 32.94) * mm, "end": v(13.6, 33.3) * mm});
            skArc(sketch, "E346.MirrorCS", {"start": v(13.6, 33.3) * mm, "mid": v(13.74, 33.65) * mm, "end": v(14.1, 33.8) * mm});
            skArc(sketch, "E347.MirrorCS", {"start": v(15.71, 33.3) * mm, "mid": v(15.56, 32.94) * mm, "end": v(15.21, 32.8) * mm});
            skLineSegment(sketch, "E348.MirrorCS", {"start": v(15.15, 32.8) * mm, "end": v(15.21, 32.8) * mm});
            skLineSegment(sketch, "E349.MirrorCS", {"start": v(15.21, 29.76) * mm, "end": v(15.15, 29.76) * mm});
            skLineSegment(sketch, "E350.MirrorCS", {"start": v(14.1, 28.76) * mm, "end": v(15.21, 28.76) * mm});
            skLineSegment(sketch, "E351.MirrorCS", {"start": v(14.15, 29.76) * mm, "end": v(14.1, 29.76) * mm});
            skLineSegment(sketch, "E352.MirrorCS", {"start": v(14.1, 32.8) * mm, "end": v(14.15, 32.8) * mm});
            skArc(sketch, "E353.MirrorCS", {"start": v(15.21, 29.76) * mm, "mid": v(15.56, 29.62) * mm, "end": v(15.71, 29.26) * mm});
            skArc(sketch, "E354.MirrorCS", {"start": v(15.21, 33.8) * mm, "mid": v(15.56, 33.65) * mm, "end": v(15.71, 33.3) * mm});
            skArc(sketch, "E355.MirrorCS", {"start": v(15.71, 29.26) * mm, "mid": v(15.56, 28.9) * mm, "end": v(15.21, 28.76) * mm});
            skArc(sketch, "E356.MirrorCS", {"start": v(14.1, 28.76) * mm, "mid": v(13.74, 28.9) * mm, "end": v(13.6, 29.26) * mm});
            skLineSegment(sketch, "E357.MirrorCS", {"start": v(15.71, 33.3) * mm, "end": v(15.71, 33.3) * mm});
            skLineSegment(sketch, "E358.MirrorCS", {"start": v(15.71, 29.26) * mm, "end": v(15.71, 29.26) * mm});
            skLineSegment(sketch, "E359.MirrorCS", {"start": v(13.6, 29.26) * mm, "end": v(13.6, 29.26) * mm});
            skLineSegment(sketch, "E360.MirrorCS", {"start": v(13.6, 33.3) * mm, "end": v(13.6, 33.3) * mm});
            skPoint(sketch, "E361.MirrorP", {"position": v(15.71, 28.76) * mm});
            skPoint(sketch, "E362.MirrorP", {"position": v(15.71, 29.76) * mm});
            skPoint(sketch, "E363.MirrorP", {"position": v(13.6, 28.76) * mm});
            skLineSegment(sketch, "E364.MirrorCS", {"start": v(15.15, 29.76) * mm, "end": v(15.15, 32.8) * mm});
            skPoint(sketch, "E365.MirrorP", {"position": v(13.6, 29.76) * mm});
            skPoint(sketch, "E366.MirrorP", {"position": v(13.6, 32.8) * mm});
            skLineSegment(sketch, "E367.MirrorCS", {"start": v(14.15, 32.8) * mm, "end": v(14.15, 29.76) * mm});
            skPoint(sketch, "E368.MirrorP", {"position": v(13.6, 33.8) * mm});
            skLineSegment(sketch, "E369.MirrorCS", {"start": v(15.21, 33.8) * mm, "end": v(14.1, 33.8) * mm});
            skPoint(sketch, "E370.MirrorP", {"position": v(15.71, 32.8) * mm});
            skPoint(sketch, "E371.MirrorP", {"position": v(15.71, 33.8) * mm});
            skLineSegment(sketch, "E372.bottom", {"start": v(-14.65, -34.75) * mm, "end": v(-13.65, -34.75) * mm});
            skLineSegment(sketch, "E372.top", {"start": v(-14.65, -37.95) * mm, "end": v(-13.65, -37.95) * mm});
            skLineSegment(sketch, "E372.left", {"start": v(-15.15, -35.25) * mm, "end": v(-15.15, -37.45) * mm});
            skLineSegment(sketch, "E372.right", {"start": v(-13.15, -35.25) * mm, "end": v(-13.15, -37.45) * mm});
            skLineSegment(sketch, "E373.bottom", {"start": v(-14.65, -41.95) * mm, "end": v(-13.65, -41.95) * mm});
            skLineSegment(sketch, "E373.top", {"start": v(-14.65, -45.15) * mm, "end": v(-13.65, -45.15) * mm});
            skLineSegment(sketch, "E373.left", {"start": v(-15.15, -42.45) * mm, "end": v(-15.15, -44.65) * mm});
            skLineSegment(sketch, "E373.right", {"start": v(-13.15, -42.45) * mm, "end": v(-13.15, -44.65) * mm});
            skLineSegment(sketch, "E374.bottom", {"start": v(-14.65, -50.15) * mm, "end": v(-13.65, -50.15) * mm});
            skLineSegment(sketch, "E374.top", {"start": v(-14.65, -53.35) * mm, "end": v(-13.65, -53.35) * mm});
            skLineSegment(sketch, "E374.left", {"start": v(-15.15, -50.65) * mm, "end": v(-15.15, -52.85) * mm});
            skLineSegment(sketch, "E374.right", {"start": v(-13.15, -50.65) * mm, "end": v(-13.15, -52.85) * mm});
            skPoint(sketch, "E375.visualSharp", {"position": v(-15.15, -34.75) * mm});
            skArc(sketch, "E375.filletArc", {"start": v(-14.65, -34.75) * mm, "mid": v(-15, -34.9) * mm, "end": v(-15.15, -35.25) * mm});
            skPoint(sketch, "E376.visualSharp", {"position": v(-13.15, -34.75) * mm});
            skArc(sketch, "E376.filletArc", {"start": v(-13.15, -35.25) * mm, "mid": v(-13.3, -34.9) * mm, "end": v(-13.65, -34.75) * mm});
            skPoint(sketch, "E377.visualSharp", {"position": v(-13.15, -37.95) * mm});
            skArc(sketch, "E377.filletArc", {"start": v(-13.65, -37.95) * mm, "mid": v(-13.3, -37.8) * mm, "end": v(-13.15, -37.45) * mm});
            skPoint(sketch, "E378.visualSharp", {"position": v(-15.15, -37.95) * mm});
            skArc(sketch, "E378.filletArc", {"start": v(-15.15, -37.45) * mm, "mid": v(-15, -37.8) * mm, "end": v(-14.65, -37.95) * mm});
            skPoint(sketch, "E379.visualSharp", {"position": v(-13.15, -41.95) * mm});
            skArc(sketch, "E379.filletArc", {"start": v(-13.15, -42.45) * mm, "mid": v(-13.3, -42.1) * mm, "end": v(-13.65, -41.95) * mm});
            skPoint(sketch, "E380.visualSharp", {"position": v(-15.15, -41.95) * mm});
            skArc(sketch, "E380.filletArc", {"start": v(-14.65, -41.95) * mm, "mid": v(-15, -42.1) * mm, "end": v(-15.15, -42.45) * mm});
            skPoint(sketch, "E381.visualSharp", {"position": v(-15.15, -45.15) * mm});
            skArc(sketch, "E381.filletArc", {"start": v(-15.15, -44.65) * mm, "mid": v(-15, -45) * mm, "end": v(-14.65, -45.15) * mm});
            skPoint(sketch, "E382.visualSharp", {"position": v(-13.15, -45.15) * mm});
            skArc(sketch, "E382.filletArc", {"start": v(-13.65, -45.15) * mm, "mid": v(-13.3, -45) * mm, "end": v(-13.15, -44.65) * mm});
            skPoint(sketch, "E383.visualSharp", {"position": v(-15.15, -50.15) * mm});
            skArc(sketch, "E383.filletArc", {"start": v(-14.65, -50.15) * mm, "mid": v(-15, -50.3) * mm, "end": v(-15.15, -50.65) * mm});
            skPoint(sketch, "E384.visualSharp", {"position": v(-13.15, -50.15) * mm});
            skArc(sketch, "E384.filletArc", {"start": v(-13.15, -50.65) * mm, "mid": v(-13.3, -50.3) * mm, "end": v(-13.65, -50.15) * mm});
            skPoint(sketch, "E385.visualSharp", {"position": v(-13.15, -53.35) * mm});
            skArc(sketch, "E385.filletArc", {"start": v(-13.65, -53.35) * mm, "mid": v(-13.3, -53.2) * mm, "end": v(-13.15, -52.85) * mm});
            skPoint(sketch, "E386.visualSharp", {"position": v(-15.15, -53.35) * mm});
            skArc(sketch, "E386.filletArc", {"start": v(-15.15, -52.85) * mm, "mid": v(-15, -53.2) * mm, "end": v(-14.65, -53.35) * mm});
            skArc(sketch, "E387.MirrorCS", {"start": v(14.65, -34.75) * mm, "mid": v(15, -34.9) * mm, "end": v(15.15, -35.25) * mm});
            skArc(sketch, "E388.MirrorCS", {"start": v(13.15, -35.25) * mm, "mid": v(13.3, -34.9) * mm, "end": v(13.65, -34.75) * mm});
            skArc(sketch, "E389.MirrorCS", {"start": v(13.65, -37.95) * mm, "mid": v(13.3, -37.8) * mm, "end": v(13.15, -37.45) * mm});
            skArc(sketch, "E390.MirrorCS", {"start": v(15.15, -37.45) * mm, "mid": v(15, -37.8) * mm, "end": v(14.65, -37.95) * mm});
            skArc(sketch, "E391.MirrorCS", {"start": v(13.15, -42.45) * mm, "mid": v(13.3, -42.1) * mm, "end": v(13.65, -41.95) * mm});
            skArc(sketch, "E392.MirrorCS", {"start": v(14.65, -41.95) * mm, "mid": v(15, -42.1) * mm, "end": v(15.15, -42.45) * mm});
            skArc(sketch, "E393.MirrorCS", {"start": v(15.15, -44.65) * mm, "mid": v(15, -45) * mm, "end": v(14.65, -45.15) * mm});
            skArc(sketch, "E394.MirrorCS", {"start": v(13.65, -45.15) * mm, "mid": v(13.3, -45) * mm, "end": v(13.15, -44.65) * mm});
            skArc(sketch, "E395.MirrorCS", {"start": v(14.65, -50.15) * mm, "mid": v(15, -50.3) * mm, "end": v(15.15, -50.65) * mm});
            skArc(sketch, "E396.MirrorCS", {"start": v(13.15, -50.65) * mm, "mid": v(13.3, -50.3) * mm, "end": v(13.65, -50.15) * mm});
            skArc(sketch, "E397.MirrorCS", {"start": v(15.15, -52.85) * mm, "mid": v(15, -53.2) * mm, "end": v(14.65, -53.35) * mm});
            skLineSegment(sketch, "E398.MirrorCS", {"start": v(14.65, -34.75) * mm, "end": v(13.65, -34.75) * mm});
            skLineSegment(sketch, "E399.MirrorCS", {"start": v(14.65, -37.95) * mm, "end": v(13.65, -37.95) * mm});
            skLineSegment(sketch, "E400.MirrorCS", {"start": v(14.65, -41.95) * mm, "end": v(13.65, -41.95) * mm});
            skLineSegment(sketch, "E401.MirrorCS", {"start": v(14.65, -45.15) * mm, "end": v(13.65, -45.15) * mm});
            skArc(sketch, "E402.MirrorCS", {"start": v(13.65, -53.35) * mm, "mid": v(13.3, -53.2) * mm, "end": v(13.15, -52.85) * mm});
            skLineSegment(sketch, "E403.MirrorCS", {"start": v(14.65, -50.15) * mm, "end": v(13.65, -50.15) * mm});
            skLineSegment(sketch, "E404.MirrorCS", {"start": v(14.65, -53.35) * mm, "end": v(13.65, -53.35) * mm});
            skLineSegment(sketch, "E405.MirrorCS", {"start": v(13.15, -50.65) * mm, "end": v(13.15, -52.85) * mm});
            skPoint(sketch, "E406.MirrorP", {"position": v(15.15, -34.75) * mm});
            skPoint(sketch, "E407.MirrorP", {"position": v(15.15, -50.15) * mm});
            skPoint(sketch, "E408.MirrorP", {"position": v(13.15, -34.75) * mm});
            skPoint(sketch, "E409.MirrorP", {"position": v(13.15, -50.15) * mm});
            skPoint(sketch, "E410.MirrorP", {"position": v(13.15, -53.35) * mm});
            skPoint(sketch, "E411.MirrorP", {"position": v(13.15, -37.95) * mm});
            skPoint(sketch, "E412.MirrorP", {"position": v(15.15, -37.95) * mm});
            skPoint(sketch, "E413.MirrorP", {"position": v(15.15, -53.35) * mm});
            skLineSegment(sketch, "E414.MirrorCS", {"start": v(15.15, -35.25) * mm, "end": v(15.15, -37.45) * mm});
            skLineSegment(sketch, "E415.MirrorCS", {"start": v(13.15, -35.25) * mm, "end": v(13.15, -37.45) * mm});
            skPoint(sketch, "E416.MirrorP", {"position": v(13.15, -41.95) * mm});
            skPoint(sketch, "E417.MirrorP", {"position": v(15.15, -41.95) * mm});
            skLineSegment(sketch, "E418.MirrorCS", {"start": v(15.15, -42.45) * mm, "end": v(15.15, -44.65) * mm});
            skPoint(sketch, "E419.MirrorP", {"position": v(15.15, -45.15) * mm});
            skLineSegment(sketch, "E420.MirrorCS", {"start": v(13.15, -42.45) * mm, "end": v(13.15, -44.65) * mm});
            skPoint(sketch, "E421.MirrorP", {"position": v(13.15, -45.15) * mm});
            skLineSegment(sketch, "E422.MirrorCS", {"start": v(15.15, -50.65) * mm, "end": v(15.15, -52.85) * mm});
            skLineSegment(sketch, "E423", {"start": v(-92.39, 132.57) * mm, "end": v(-92.39, 102.87) * mm, "construction": true});
            skLineSegment(sketch, "E424", {"start": v(-106.44, 118.17) * mm, "end": v(-78.74, 118.17) * mm, "construction": true});
            skLineSegment(sketch, "E425", {"start": v(-83.09, 127.47) * mm, "end": v(-101.69, 108.87) * mm, "construction": true});
            skLineSegment(sketch, "E426.MirrorCS", {"start": v(-101.69, 127.47) * mm, "end": v(-83.09, 108.87) * mm, "construction": true});
            skArc(sketch, "E427", {"start": v(-93.99, 126.17) * mm, "mid": v(-92.39, 124.57) * mm, "end": v(-90.79, 126.17) * mm});
            skLineSegment(sketch, "E428", {"start": v(-93.99, 127.67) * mm, "end": v(-93.99, 126.17) * mm});
            skLineSegment(sketch, "E429.MirrorCS", {"start": v(-90.79, 127.67) * mm, "end": v(-90.79, 126.17) * mm});
            skArc(sketch, "E430.trimOffspring", {"start": v(-90.79, 127.67) * mm, "mid": v(-92.39, 129.27) * mm, "end": v(-93.99, 127.67) * mm});
            skLineSegment(sketch, "E431.MirrorCS", {"start": v(-101.89, 119.77) * mm, "end": v(-100.39, 119.77) * mm});
            skArc(sketch, "E432.MirrorCS", {"start": v(-101.89, 116.57) * mm, "mid": v(-103.49, 118.17) * mm, "end": v(-101.89, 119.77) * mm});
            skLineSegment(sketch, "E433.MirrorCS", {"start": v(-101.89, 116.57) * mm, "end": v(-100.39, 116.57) * mm});
            skArc(sketch, "E434.MirrorCS", {"start": v(-100.39, 119.77) * mm, "mid": v(-98.79, 118.17) * mm, "end": v(-100.39, 116.57) * mm});
            skArc(sketch, "E435.MirrorCS", {"start": v(-84.39, 119.77) * mm, "mid": v(-85.99, 118.17) * mm, "end": v(-84.39, 116.57) * mm});
            skLineSegment(sketch, "E436.MirrorCS", {"start": v(-82.89, 119.77) * mm, "end": v(-84.39, 119.77) * mm});
            skLineSegment(sketch, "E437.MirrorCS", {"start": v(-82.89, 116.57) * mm, "end": v(-84.39, 116.57) * mm});
            skArc(sketch, "E438.MirrorCS", {"start": v(-82.89, 116.57) * mm, "mid": v(-81.29, 118.17) * mm, "end": v(-82.89, 119.77) * mm});
            skArc(sketch, "E439.MirrorCS", {"start": v(-93.99, 110.17) * mm, "mid": v(-92.39, 111.77) * mm, "end": v(-90.79, 110.17) * mm});
            skLineSegment(sketch, "E440.MirrorCS", {"start": v(-93.99, 108.67) * mm, "end": v(-93.99, 110.17) * mm});
            skArc(sketch, "E441.MirrorCS", {"start": v(-90.79, 108.67) * mm, "mid": v(-92.39, 107.07) * mm, "end": v(-93.99, 108.67) * mm});
            skLineSegment(sketch, "E442.MirrorCS", {"start": v(-90.79, 108.67) * mm, "end": v(-90.79, 110.17) * mm});
            skArc(sketch, "E443", {"start": v(-95.92, 123.12) * mm, "mid": v(-97.34, 123.12) * mm, "end": v(-97.34, 121.7) * mm});
            skLineSegment(sketch, "E444", {"start": v(-95.92, 123.12) * mm, "end": v(-93.52, 120.72) * mm});
            skLineSegment(sketch, "E445.MirrorCS", {"start": v(-97.34, 121.7) * mm, "end": v(-94.93, 119.3) * mm});
            skLineSegment(sketch, "E446.MirrorCS", {"start": v(-88.85, 123.12) * mm, "end": v(-91.26, 120.72) * mm});
            skArc(sketch, "E447.MirrorCS", {"start": v(-88.85, 123.12) * mm, "mid": v(-87.44, 123.12) * mm, "end": v(-87.44, 121.7) * mm});
            skLineSegment(sketch, "E448.MirrorCS", {"start": v(-87.44, 121.7) * mm, "end": v(-89.84, 119.3) * mm});
            skLineSegment(sketch, "E449.MirrorCS", {"start": v(-97.34, 114.64) * mm, "end": v(-94.93, 117.04) * mm});
            skArc(sketch, "E450.MirrorCS", {"start": v(-95.92, 113.22) * mm, "mid": v(-97.34, 113.22) * mm, "end": v(-97.34, 114.64) * mm});
            skLineSegment(sketch, "E451.MirrorCS", {"start": v(-95.92, 113.22) * mm, "end": v(-93.52, 115.63) * mm});
            skLineSegment(sketch, "E452.MirrorCS", {"start": v(-88.85, 113.22) * mm, "end": v(-91.26, 115.63) * mm});
            skArc(sketch, "E453.MirrorCS", {"start": v(-88.85, 113.22) * mm, "mid": v(-87.44, 113.22) * mm, "end": v(-87.44, 114.64) * mm});
            skLineSegment(sketch, "E454.MirrorCS", {"start": v(-87.44, 114.64) * mm, "end": v(-89.84, 117.04) * mm});
            skArc(sketch, "E455.trimOffspring", {"start": v(-91.74, 120.59) * mm, "mid": v(-92.39, 120.67) * mm, "end": v(-93.03, 120.59) * mm});
            skArc(sketch, "E456.trimOffspring", {"start": v(-89.97, 117.53) * mm, "mid": v(-89.89, 118.17) * mm, "end": v(-89.97, 118.82) * mm});
            skArc(sketch, "E457.trimOffspring", {"start": v(-93.03, 115.76) * mm, "mid": v(-92.39, 115.67) * mm, "end": v(-91.74, 115.76) * mm});
            skPoint(sketch, "E458.visualSharp", {"position": v(-94.71, 117.26) * mm});
            skArc(sketch, "E458.filletArc", {"start": v(-94.93, 117.04) * mm, "mid": v(-94.8, 117.27) * mm, "end": v(-94.8, 117.53) * mm});
            skPoint(sketch, "E459.visualSharp", {"position": v(-94.71, 119.09) * mm});
            skArc(sketch, "E459.filletArc", {"start": v(-94.8, 118.82) * mm, "mid": v(-94.8, 119.08) * mm, "end": v(-94.93, 119.3) * mm});
            skPoint(sketch, "E460.visualSharp", {"position": v(-93.3, 120.5) * mm});
            skArc(sketch, "E460.filletArc", {"start": v(-93.52, 120.72) * mm, "mid": v(-93.3, 120.59) * mm, "end": v(-93.03, 120.59) * mm});
            skPoint(sketch, "E461.visualSharp", {"position": v(-91.47, 120.5) * mm});
            skArc(sketch, "E461.filletArc", {"start": v(-91.74, 120.59) * mm, "mid": v(-91.48, 120.59) * mm, "end": v(-91.26, 120.72) * mm});
            skPoint(sketch, "E462.visualSharp", {"position": v(-90.06, 119.09) * mm});
            skArc(sketch, "E462.filletArc", {"start": v(-89.84, 119.3) * mm, "mid": v(-89.97, 119.08) * mm, "end": v(-89.97, 118.82) * mm});
            skPoint(sketch, "E463.visualSharp", {"position": v(-90.06, 117.26) * mm});
            skArc(sketch, "E463.filletArc", {"start": v(-89.97, 117.53) * mm, "mid": v(-89.97, 117.27) * mm, "end": v(-89.84, 117.04) * mm});
            skPoint(sketch, "E464.visualSharp", {"position": v(-91.47, 115.84) * mm});
            skArc(sketch, "E464.filletArc", {"start": v(-91.26, 115.63) * mm, "mid": v(-91.48, 115.76) * mm, "end": v(-91.74, 115.76) * mm});
            skPoint(sketch, "E465.visualSharp", {"position": v(-93.3, 115.84) * mm});
            skArc(sketch, "E465.filletArc", {"start": v(-93.03, 115.76) * mm, "mid": v(-93.3, 115.76) * mm, "end": v(-93.52, 115.63) * mm});
            skArc(sketch, "E466.MirrorCS", {"start": v(89.97, 117.53) * mm, "mid": v(89.89, 118.17) * mm, "end": v(89.97, 118.82) * mm});
            skArc(sketch, "E467.MirrorCS", {"start": v(94.93, 117.04) * mm, "mid": v(94.8, 117.27) * mm, "end": v(94.8, 117.53) * mm});
            skArc(sketch, "E468.MirrorCS", {"start": v(94.8, 118.82) * mm, "mid": v(94.8, 119.08) * mm, "end": v(94.93, 119.3) * mm});
            skArc(sketch, "E469.MirrorCS", {"start": v(91.74, 120.59) * mm, "mid": v(91.48, 120.59) * mm, "end": v(91.26, 120.72) * mm});
            skArc(sketch, "E470.MirrorCS", {"start": v(89.84, 119.3) * mm, "mid": v(89.97, 119.08) * mm, "end": v(89.97, 118.82) * mm});
            skArc(sketch, "E471.MirrorCS", {"start": v(89.97, 117.53) * mm, "mid": v(89.97, 117.27) * mm, "end": v(89.84, 117.04) * mm});
            skArc(sketch, "E472.MirrorCS", {"start": v(94.8, 118.82) * mm, "mid": v(94.89, 118.17) * mm, "end": v(94.8, 117.53) * mm});
            skArc(sketch, "E473.MirrorCS", {"start": v(91.74, 120.59) * mm, "mid": v(92.39, 120.67) * mm, "end": v(93.03, 120.59) * mm});
            skArc(sketch, "E474.MirrorCS", {"start": v(93.03, 115.76) * mm, "mid": v(92.39, 115.67) * mm, "end": v(91.74, 115.76) * mm});
            skArc(sketch, "E475.MirrorCS", {"start": v(93.52, 120.72) * mm, "mid": v(93.3, 120.59) * mm, "end": v(93.03, 120.59) * mm});
            skArc(sketch, "E476.MirrorCS", {"start": v(91.26, 115.63) * mm, "mid": v(91.48, 115.76) * mm, "end": v(91.74, 115.76) * mm});
            skArc(sketch, "E477.MirrorCS", {"start": v(93.03, 115.76) * mm, "mid": v(93.3, 115.76) * mm, "end": v(93.52, 115.63) * mm});
            skPoint(sketch, "E478.MirrorP", {"position": v(90.06, 119.09) * mm});
            skLineSegment(sketch, "E479.MirrorCS", {"start": v(88.85, 113.22) * mm, "end": v(91.26, 115.63) * mm});
            skLineSegment(sketch, "E480.MirrorCS", {"start": v(82.89, 119.77) * mm, "end": v(84.39, 119.77) * mm});
            skLineSegment(sketch, "E481.MirrorCS", {"start": v(82.89, 116.57) * mm, "end": v(84.39, 116.57) * mm});
            skArc(sketch, "E482.MirrorCS", {"start": v(88.85, 113.22) * mm, "mid": v(87.44, 113.22) * mm, "end": v(87.44, 114.64) * mm});
            skLineSegment(sketch, "E483.MirrorCS", {"start": v(87.44, 114.64) * mm, "end": v(89.84, 117.04) * mm});
            skArc(sketch, "E484.MirrorCS", {"start": v(82.89, 116.57) * mm, "mid": v(81.29, 118.17) * mm, "end": v(82.89, 119.77) * mm});
            skArc(sketch, "E485.MirrorCS", {"start": v(93.99, 110.17) * mm, "mid": v(92.39, 111.77) * mm, "end": v(90.79, 110.17) * mm});
            skPoint(sketch, "E486.MirrorP", {"position": v(94.71, 117.26) * mm});
            skLineSegment(sketch, "E487.MirrorCS", {"start": v(93.99, 108.67) * mm, "end": v(93.99, 110.17) * mm});
            skArc(sketch, "E488.MirrorCS", {"start": v(90.79, 108.67) * mm, "mid": v(92.39, 107.07) * mm, "end": v(93.99, 108.67) * mm});
            skLineSegment(sketch, "E489.MirrorCS", {"start": v(83.09, 127.47) * mm, "end": v(101.69, 108.87) * mm, "construction": true});
            skLineSegment(sketch, "E490.MirrorCS", {"start": v(90.79, 108.67) * mm, "end": v(90.79, 110.17) * mm});
            skLineSegment(sketch, "E491.MirrorCS", {"start": v(101.69, 127.47) * mm, "end": v(83.09, 108.87) * mm, "construction": true});
            skArc(sketch, "E492.MirrorCS", {"start": v(95.92, 123.12) * mm, "mid": v(97.34, 123.12) * mm, "end": v(97.34, 121.7) * mm});
            skArc(sketch, "E493.MirrorCS", {"start": v(93.99, 126.17) * mm, "mid": v(92.39, 124.57) * mm, "end": v(90.79, 126.17) * mm});
            skLineSegment(sketch, "E494.MirrorCS", {"start": v(93.99, 127.67) * mm, "end": v(93.99, 126.17) * mm});
            skLineSegment(sketch, "E495.MirrorCS", {"start": v(95.92, 123.12) * mm, "end": v(93.52, 120.72) * mm});
            skLineSegment(sketch, "E496.MirrorCS", {"start": v(90.79, 127.67) * mm, "end": v(90.79, 126.17) * mm});
            skLineSegment(sketch, "E497.MirrorCS", {"start": v(97.34, 121.7) * mm, "end": v(94.93, 119.3) * mm});
            skArc(sketch, "E498.MirrorCS", {"start": v(90.79, 127.67) * mm, "mid": v(92.39, 129.27) * mm, "end": v(93.99, 127.67) * mm});
            skLineSegment(sketch, "E499.MirrorCS", {"start": v(88.85, 123.12) * mm, "end": v(91.26, 120.72) * mm});
            skLineSegment(sketch, "E500.MirrorCS", {"start": v(101.89, 119.77) * mm, "end": v(100.39, 119.77) * mm});
            skArc(sketch, "E501.MirrorCS", {"start": v(88.85, 123.12) * mm, "mid": v(87.44, 123.12) * mm, "end": v(87.44, 121.7) * mm});
            skArc(sketch, "E502.MirrorCS", {"start": v(101.89, 116.57) * mm, "mid": v(103.49, 118.17) * mm, "end": v(101.89, 119.77) * mm});
            skPoint(sketch, "E503.MirrorP", {"position": v(94.71, 119.09) * mm});
            skLineSegment(sketch, "E504.MirrorCS", {"start": v(87.44, 121.7) * mm, "end": v(89.84, 119.3) * mm});
            skLineSegment(sketch, "E505.MirrorCS", {"start": v(101.89, 116.57) * mm, "end": v(100.39, 116.57) * mm});
            skLineSegment(sketch, "E506.MirrorCS", {"start": v(97.34, 114.64) * mm, "end": v(94.93, 117.04) * mm});
            skPoint(sketch, "E507.MirrorP", {"position": v(90.06, 117.26) * mm});
            skPoint(sketch, "E508.MirrorP", {"position": v(91.47, 120.5) * mm});
            skPoint(sketch, "E509.MirrorP", {"position": v(91.47, 115.84) * mm});
            skPoint(sketch, "E510.MirrorP", {"position": v(93.3, 115.84) * mm});
            skPoint(sketch, "E511.MirrorP", {"position": v(93.3, 120.5) * mm});
            skLineSegment(sketch, "E512.MirrorCS", {"start": v(95.92, 113.22) * mm, "end": v(93.52, 115.63) * mm});
            skArc(sketch, "E513.MirrorCS", {"start": v(84.39, 119.77) * mm, "mid": v(85.99, 118.17) * mm, "end": v(84.39, 116.57) * mm});
            skArc(sketch, "E514.MirrorCS", {"start": v(95.92, 113.22) * mm, "mid": v(97.34, 113.22) * mm, "end": v(97.34, 114.64) * mm});
            skArc(sketch, "E515.MirrorCS", {"start": v(100.39, 119.77) * mm, "mid": v(98.79, 118.17) * mm, "end": v(100.39, 116.57) * mm});
            skArc(sketch, "E516.MirrorCS", {"start": v(-89.84, -119.3) * mm, "mid": v(-89.97, -119.08) * mm, "end": v(-89.97, -118.82) * mm});
            skArc(sketch, "E517.MirrorCS", {"start": v(-91.74, -120.59) * mm, "mid": v(-91.48, -120.59) * mm, "end": v(-91.26, -120.72) * mm});
            skArc(sketch, "E518.MirrorCS", {"start": v(-94.8, -118.82) * mm, "mid": v(-94.8, -119.08) * mm, "end": v(-94.93, -119.3) * mm});
            skArc(sketch, "E519.MirrorCS", {"start": v(-94.93, -117.04) * mm, "mid": v(-94.8, -117.27) * mm, "end": v(-94.8, -117.53) * mm});
            skArc(sketch, "E520.MirrorCS", {"start": v(-89.97, -117.53) * mm, "mid": v(-89.89, -118.17) * mm, "end": v(-89.97, -118.82) * mm});
            skArc(sketch, "E521.MirrorCS", {"start": v(-89.97, -117.53) * mm, "mid": v(-89.97, -117.27) * mm, "end": v(-89.84, -117.04) * mm});
            skArc(sketch, "E522.MirrorCS", {"start": v(-91.26, -115.63) * mm, "mid": v(-91.48, -115.76) * mm, "end": v(-91.74, -115.76) * mm});
            skArc(sketch, "E523.MirrorCS", {"start": v(-94.8, -118.82) * mm, "mid": v(-94.89, -118.17) * mm, "end": v(-94.8, -117.53) * mm});
            skArc(sketch, "E524.MirrorCS", {"start": v(-93.52, -120.72) * mm, "mid": v(-93.3, -120.59) * mm, "end": v(-93.03, -120.59) * mm});
            skArc(sketch, "E525.MirrorCS", {"start": v(-91.74, -120.59) * mm, "mid": v(-92.39, -120.67) * mm, "end": v(-93.03, -120.59) * mm});
            skLineSegment(sketch, "E526.MirrorCS", {"start": v(-93.99, -127.67) * mm, "end": v(-93.99, -126.17) * mm});
            skArc(sketch, "E527.MirrorCS", {"start": v(-93.03, -115.76) * mm, "mid": v(-92.39, -115.67) * mm, "end": v(-91.74, -115.76) * mm});
            skArc(sketch, "E528.MirrorCS", {"start": v(-93.03, -115.76) * mm, "mid": v(-93.3, -115.76) * mm, "end": v(-93.52, -115.63) * mm});
            skPoint(sketch, "E529.MirrorP", {"position": v(-93.3, -115.84) * mm});
            skLineSegment(sketch, "E530.MirrorCS", {"start": v(-88.85, -123.12) * mm, "end": v(-91.26, -120.72) * mm});
            skLineSegment(sketch, "E531.MirrorCS", {"start": v(-97.34, -121.7) * mm, "end": v(-94.93, -119.3) * mm});
            skLineSegment(sketch, "E532.MirrorCS", {"start": v(-90.79, -127.67) * mm, "end": v(-90.79, -126.17) * mm});
            skPoint(sketch, "E533.MirrorP", {"position": v(-91.47, -120.5) * mm});
            skPoint(sketch, "E534.MirrorP", {"position": v(-93.3, -120.5) * mm});
            skLineSegment(sketch, "E535.MirrorCS", {"start": v(-87.44, -121.7) * mm, "end": v(-89.84, -119.3) * mm});
            skPoint(sketch, "E536.MirrorP", {"position": v(-94.71, -119.09) * mm});
            skLineSegment(sketch, "E537.MirrorCS", {"start": v(-101.89, -119.77) * mm, "end": v(-100.39, -119.77) * mm});
            skPoint(sketch, "E538.MirrorP", {"position": v(-90.06, -119.09) * mm});
            skLineSegment(sketch, "E539.MirrorCS", {"start": v(-95.92, -123.12) * mm, "end": v(-93.52, -120.72) * mm});
            skArc(sketch, "E540.MirrorCS", {"start": v(-95.92, -123.12) * mm, "mid": v(-97.34, -123.12) * mm, "end": v(-97.34, -121.7) * mm});
            skLineSegment(sketch, "E541.MirrorCS", {"start": v(-90.79, -108.67) * mm, "end": v(-90.79, -110.17) * mm});
            skLineSegment(sketch, "E542.MirrorCS", {"start": v(-93.99, -108.67) * mm, "end": v(-93.99, -110.17) * mm});
            skArc(sketch, "E543.MirrorCS", {"start": v(-82.89, -116.57) * mm, "mid": v(-81.29, -118.17) * mm, "end": v(-82.89, -119.77) * mm});
            skLineSegment(sketch, "E544.MirrorCS", {"start": v(-87.44, -114.64) * mm, "end": v(-89.84, -117.04) * mm});
            skLineSegment(sketch, "E545.MirrorCS", {"start": v(-82.89, -116.57) * mm, "end": v(-84.39, -116.57) * mm});
            skArc(sketch, "E546.MirrorCS", {"start": v(-88.85, -113.22) * mm, "mid": v(-87.44, -113.22) * mm, "end": v(-87.44, -114.64) * mm});
            skLineSegment(sketch, "E547.MirrorCS", {"start": v(-88.85, -113.22) * mm, "end": v(-91.26, -115.63) * mm});
            skLineSegment(sketch, "E548.MirrorCS", {"start": v(-82.89, -119.77) * mm, "end": v(-84.39, -119.77) * mm});
            skArc(sketch, "E549.MirrorCS", {"start": v(-84.39, -119.77) * mm, "mid": v(-85.99, -118.17) * mm, "end": v(-84.39, -116.57) * mm});
            skLineSegment(sketch, "E550.MirrorCS", {"start": v(-95.92, -113.22) * mm, "end": v(-93.52, -115.63) * mm});
            skArc(sketch, "E551.MirrorCS", {"start": v(-95.92, -113.22) * mm, "mid": v(-97.34, -113.22) * mm, "end": v(-97.34, -114.64) * mm});
            skPoint(sketch, "E552.MirrorP", {"position": v(-90.06, -117.26) * mm});
            skArc(sketch, "E553.MirrorCS", {"start": v(-88.85, -123.12) * mm, "mid": v(-87.44, -123.12) * mm, "end": v(-87.44, -121.7) * mm});
            skLineSegment(sketch, "E554.MirrorCS", {"start": v(-101.89, -116.57) * mm, "end": v(-100.39, -116.57) * mm});
            skLineSegment(sketch, "E555.MirrorCS", {"start": v(-97.34, -114.64) * mm, "end": v(-94.93, -117.04) * mm});
            skPoint(sketch, "E556.MirrorP", {"position": v(-91.47, -115.84) * mm});
            skPoint(sketch, "E557.MirrorP", {"position": v(-94.71, -117.26) * mm});
            skArc(sketch, "E558.MirrorCS", {"start": v(-93.99, -126.17) * mm, "mid": v(-92.39, -124.57) * mm, "end": v(-90.79, -126.17) * mm});
            skArc(sketch, "E559.MirrorCS", {"start": v(-93.99, -110.17) * mm, "mid": v(-92.39, -111.77) * mm, "end": v(-90.79, -110.17) * mm});
            skArc(sketch, "E560.MirrorCS", {"start": v(-100.39, -119.77) * mm, "mid": v(-98.79, -118.17) * mm, "end": v(-100.39, -116.57) * mm});
            skPoint(sketch, "E561.MirrorP", {"position": v(-82.26, -129.24) * mm});
            skArc(sketch, "E562.MirrorCS", {"start": v(-90.79, -127.67) * mm, "mid": v(-92.39, -129.27) * mm, "end": v(-93.99, -127.67) * mm});
            skLineSegment(sketch, "E563.MirrorCS", {"start": v(-101.69, -127.47) * mm, "end": v(-83.09, -108.87) * mm, "construction": true});
            skLineSegment(sketch, "E564.MirrorCS", {"start": v(-83.09, -127.47) * mm, "end": v(-101.69, -108.87) * mm, "construction": true});
            skArc(sketch, "E565.MirrorCS", {"start": v(-90.79, -108.67) * mm, "mid": v(-92.39, -107.07) * mm, "end": v(-93.99, -108.67) * mm});
            skLineSegment(sketch, "E566.MirrorCS", {"start": v(-106.44, -118.17) * mm, "end": v(-78.74, -118.17) * mm, "construction": true});
            skArc(sketch, "E567.MirrorCS", {"start": v(-101.89, -116.57) * mm, "mid": v(-103.49, -118.17) * mm, "end": v(-101.89, -119.77) * mm});
            skArc(sketch, "E568.MirrorCS", {"start": v(91.74, -120.59) * mm, "mid": v(91.48, -120.59) * mm, "end": v(91.26, -120.72) * mm});
            skArc(sketch, "E569.MirrorCS", {"start": v(89.97, -117.53) * mm, "mid": v(89.89, -118.17) * mm, "end": v(89.97, -118.82) * mm});
            skArc(sketch, "E570.MirrorCS", {"start": v(94.8, -118.82) * mm, "mid": v(94.89, -118.17) * mm, "end": v(94.8, -117.53) * mm});
            skArc(sketch, "E571.MirrorCS", {"start": v(91.74, -120.59) * mm, "mid": v(92.39, -120.67) * mm, "end": v(93.03, -120.59) * mm});
            skArc(sketch, "E572.MirrorCS", {"start": v(93.52, -120.72) * mm, "mid": v(93.3, -120.59) * mm, "end": v(93.03, -120.59) * mm});
            skArc(sketch, "E573.MirrorCS", {"start": v(94.93, -117.04) * mm, "mid": v(94.8, -117.27) * mm, "end": v(94.8, -117.53) * mm});
            skArc(sketch, "E574.MirrorCS", {"start": v(94.8, -118.82) * mm, "mid": v(94.8, -119.08) * mm, "end": v(94.93, -119.3) * mm});
            skArc(sketch, "E575.MirrorCS", {"start": v(89.84, -119.3) * mm, "mid": v(89.97, -119.08) * mm, "end": v(89.97, -118.82) * mm});
            skArc(sketch, "E576.MirrorCS", {"start": v(89.97, -117.53) * mm, "mid": v(89.97, -117.27) * mm, "end": v(89.84, -117.04) * mm});
            skArc(sketch, "E577.MirrorCS", {"start": v(93.03, -115.76) * mm, "mid": v(92.39, -115.67) * mm, "end": v(91.74, -115.76) * mm});
            skArc(sketch, "E578.MirrorCS", {"start": v(91.26, -115.63) * mm, "mid": v(91.48, -115.76) * mm, "end": v(91.74, -115.76) * mm});
            skArc(sketch, "E579.MirrorCS", {"start": v(93.03, -115.76) * mm, "mid": v(93.3, -115.76) * mm, "end": v(93.52, -115.63) * mm});
            skArc(sketch, "E580.MirrorCS", {"start": v(82.89, -116.57) * mm, "mid": v(81.29, -118.17) * mm, "end": v(82.89, -119.77) * mm});
            skArc(sketch, "E581.MirrorCS", {"start": v(88.85, -123.12) * mm, "mid": v(87.44, -123.12) * mm, "end": v(87.44, -121.7) * mm});
            skLineSegment(sketch, "E582.MirrorCS", {"start": v(93.99, -108.67) * mm, "end": v(93.99, -110.17) * mm});
            skArc(sketch, "E583.MirrorCS", {"start": v(101.89, -116.57) * mm, "mid": v(103.49, -118.17) * mm, "end": v(101.89, -119.77) * mm});
            skLineSegment(sketch, "E584.MirrorCS", {"start": v(87.44, -121.7) * mm, "end": v(89.84, -119.3) * mm});
            skLineSegment(sketch, "E585.MirrorCS", {"start": v(101.89, -116.57) * mm, "end": v(100.39, -116.57) * mm});
            skLineSegment(sketch, "E586.MirrorCS", {"start": v(97.34, -114.64) * mm, "end": v(94.93, -117.04) * mm});
            skLineSegment(sketch, "E587.MirrorCS", {"start": v(90.79, -108.67) * mm, "end": v(90.79, -110.17) * mm});
            skLineSegment(sketch, "E588.MirrorCS", {"start": v(95.92, -113.22) * mm, "end": v(93.52, -115.63) * mm});
            skArc(sketch, "E589.MirrorCS", {"start": v(84.39, -119.77) * mm, "mid": v(85.99, -118.17) * mm, "end": v(84.39, -116.57) * mm});
            skArc(sketch, "E590.MirrorCS", {"start": v(95.92, -123.12) * mm, "mid": v(97.34, -123.12) * mm, "end": v(97.34, -121.7) * mm});
            skArc(sketch, "E591.MirrorCS", {"start": v(95.92, -113.22) * mm, "mid": v(97.34, -113.22) * mm, "end": v(97.34, -114.64) * mm});
            skArc(sketch, "E592.MirrorCS", {"start": v(100.39, -119.77) * mm, "mid": v(98.79, -118.17) * mm, "end": v(100.39, -116.57) * mm});
            skLineSegment(sketch, "E593.MirrorCS", {"start": v(93.99, -127.67) * mm, "end": v(93.99, -126.17) * mm});
            skLineSegment(sketch, "E594.MirrorCS", {"start": v(88.85, -113.22) * mm, "end": v(91.26, -115.63) * mm});
            skLineSegment(sketch, "E595.MirrorCS", {"start": v(95.92, -123.12) * mm, "end": v(93.52, -120.72) * mm});
            skLineSegment(sketch, "E596.MirrorCS", {"start": v(82.89, -119.77) * mm, "end": v(84.39, -119.77) * mm});
            skPoint(sketch, "E597.MirrorP", {"position": v(93.3, -120.5) * mm});
            skLineSegment(sketch, "E598.MirrorCS", {"start": v(82.89, -116.57) * mm, "end": v(84.39, -116.57) * mm});
            skLineSegment(sketch, "E599.MirrorCS", {"start": v(90.79, -127.67) * mm, "end": v(90.79, -126.17) * mm});
            skArc(sketch, "E600.MirrorCS", {"start": v(88.85, -113.22) * mm, "mid": v(87.44, -113.22) * mm, "end": v(87.44, -114.64) * mm});
            skLineSegment(sketch, "E601.MirrorCS", {"start": v(97.34, -121.7) * mm, "end": v(94.93, -119.3) * mm});
            skPoint(sketch, "E602.MirrorP", {"position": v(91.47, -120.5) * mm});
            skPoint(sketch, "E603.MirrorP", {"position": v(93.3, -115.84) * mm});
            skLineSegment(sketch, "E604.MirrorCS", {"start": v(87.44, -114.64) * mm, "end": v(89.84, -117.04) * mm});
            skPoint(sketch, "E605.MirrorP", {"position": v(90.06, -117.26) * mm});
            skPoint(sketch, "E606.MirrorP", {"position": v(94.71, -117.26) * mm});
            skPoint(sketch, "E607.MirrorP", {"position": v(91.47, -115.84) * mm});
            skArc(sketch, "E608.MirrorCS", {"start": v(93.99, -110.17) * mm, "mid": v(92.39, -111.77) * mm, "end": v(90.79, -110.17) * mm});
            skLineSegment(sketch, "E609.MirrorCS", {"start": v(101.89, -119.77) * mm, "end": v(100.39, -119.77) * mm});
            skLineSegment(sketch, "E610.MirrorCS", {"start": v(88.85, -123.12) * mm, "end": v(91.26, -120.72) * mm});
            skPoint(sketch, "E611.MirrorP", {"position": v(94.71, -119.09) * mm});
            skPoint(sketch, "E612.MirrorP", {"position": v(82.26, -129.24) * mm});
            skPoint(sketch, "E613.MirrorP", {"position": v(90.06, -119.09) * mm});
            skArc(sketch, "E614.MirrorCS", {"start": v(90.79, -108.67) * mm, "mid": v(92.39, -107.07) * mm, "end": v(93.99, -108.67) * mm});
            skLineSegment(sketch, "E615.MirrorCS", {"start": v(83.09, -127.47) * mm, "end": v(101.69, -108.87) * mm, "construction": true});
            skLineSegment(sketch, "E616.MirrorCS", {"start": v(101.69, -127.47) * mm, "end": v(83.09, -108.87) * mm, "construction": true});
            skArc(sketch, "E617.MirrorCS", {"start": v(93.99, -126.17) * mm, "mid": v(92.39, -124.57) * mm, "end": v(90.79, -126.17) * mm});
            skArc(sketch, "E618.MirrorCS", {"start": v(90.79, -127.67) * mm, "mid": v(92.39, -129.27) * mm, "end": v(93.99, -127.67) * mm});
            skSolve(sketch);
        }
        {
            var Q0;
            Q0 = qSketchRegion(id + "F0", true);
            extrude(context, id + "F1", {"entities" : qUnion([Q0]), "depth" : 4 * mm, "offsetDistance" : 25 * mm});
        }
    });
